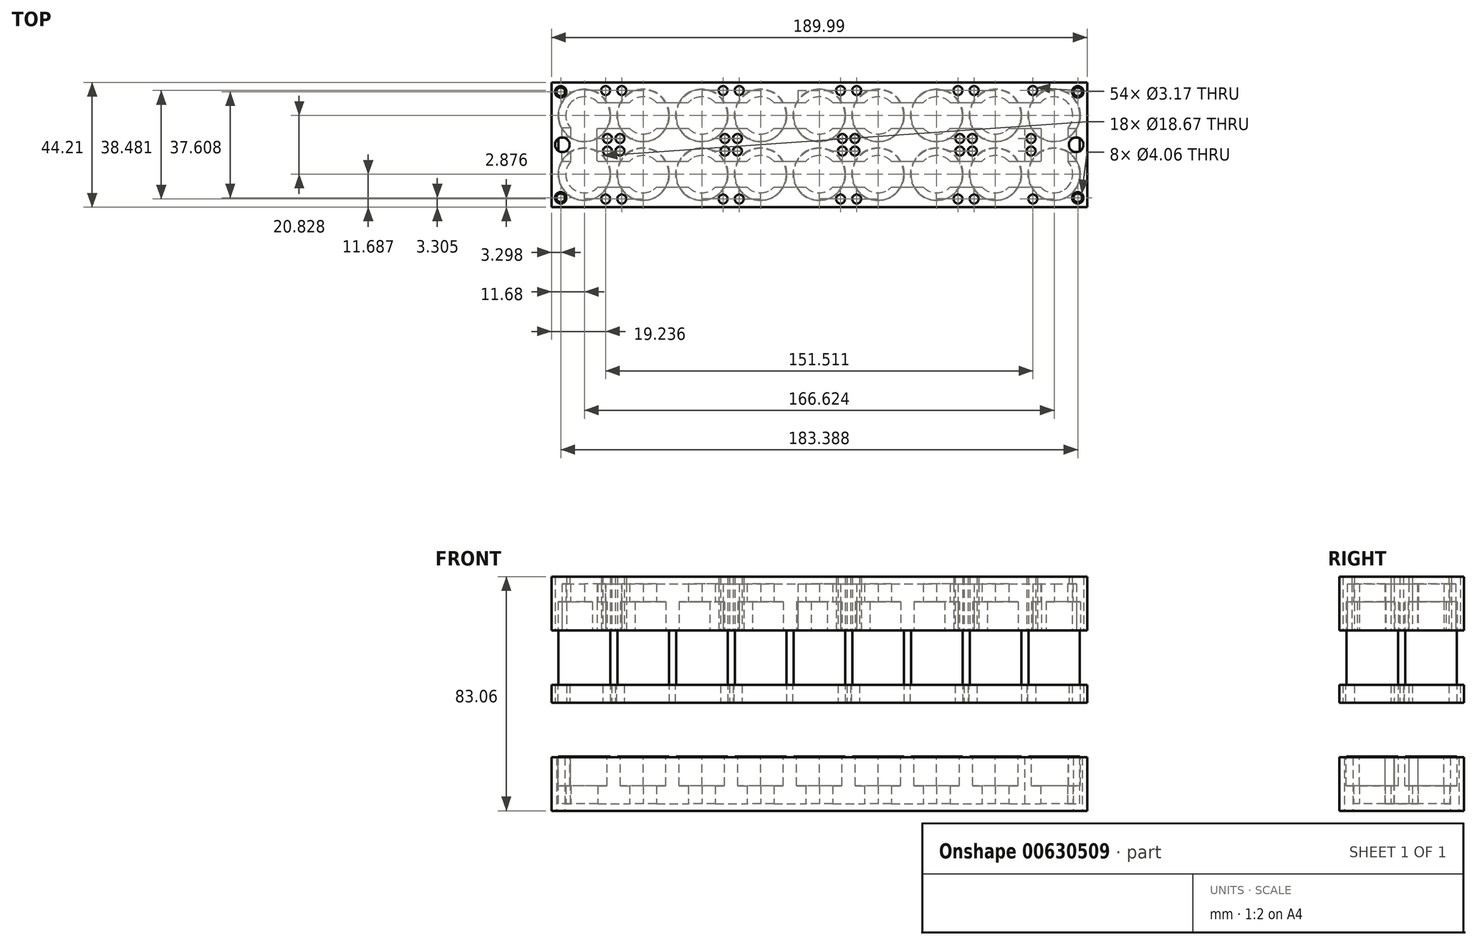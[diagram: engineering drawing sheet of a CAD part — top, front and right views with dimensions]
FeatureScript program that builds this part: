
annotation { "Feature Type Name" : "Feature", "Feature Type Description" : "" }
export const myFeature = defineFeature(function(context is Context, id is Id, definition is map)
    precondition{}
    {
        {
            var Q0;
            Q0=qCreatedBy(makeId("Top.planeOp"),FACE);
            var sketch = newSketch(context, id + "F0", { "sketchPlane" : qUnion([Q0])});
            skCircle(sketch, "E0", {"center": v(0, 0) * mm, "radius": 9.14 * mm});
            skCircle(sketch, "E1.1.0.0", {"center": v(20.83, 0) * mm, "radius": 9.14 * mm});
            skCircle(sketch, "E1.2.0.0", {"center": v(41.66, 0) * mm, "radius": 9.14 * mm});
            skCircle(sketch, "E1.3.0.0", {"center": v(62.48, 0) * mm, "radius": 9.14 * mm});
            skCircle(sketch, "E1.4.0.0", {"center": v(83.31, 0) * mm, "radius": 9.14 * mm});
            skCircle(sketch, "E1.5.0.0", {"center": v(104.14, 0) * mm, "radius": 9.14 * mm});
            skLineSegment(sketch, "E1.direction1", {"start": v(0, 0) * mm, "end": v(20.83, 0) * mm, "construction": true});
            skCircle(sketch, "E2", {"center": v(0, 20.83) * mm, "radius": 9.14 * mm});
            skCircle(sketch, "E3.1.0.0", {"center": v(20.83, 20.83) * mm, "radius": 9.14 * mm});
            skCircle(sketch, "E3.2.0.0", {"center": v(41.66, 20.83) * mm, "radius": 9.14 * mm});
            skCircle(sketch, "E3.3.0.0", {"center": v(62.48, 20.83) * mm, "radius": 9.14 * mm});
            skCircle(sketch, "E3.4.0.0", {"center": v(83.31, 20.83) * mm, "radius": 9.14 * mm});
            skCircle(sketch, "E3.5.0.0", {"center": v(104.14, 20.83) * mm, "radius": 9.14 * mm});
            skLineSegment(sketch, "E3.direction1", {"start": v(0, 20.83) * mm, "end": v(20.83, 20.83) * mm, "construction": true});
            skCircle(sketch, "E4.0.6.0", {"center": v(124.97, 20.83) * mm, "radius": 9.14 * mm});
            skCircle(sketch, "E4.0.7.0", {"center": v(145.8, 20.83) * mm, "radius": 9.14 * mm});
            skCircle(sketch, "E4.0.8.0", {"center": v(166.62, 20.83) * mm, "radius": 9.14 * mm});
            skCircle(sketch, "E5.0.6.0", {"center": v(124.97, 0) * mm, "radius": 9.14 * mm});
            skCircle(sketch, "E5.0.7.0", {"center": v(145.8, 0) * mm, "radius": 9.14 * mm});
            skCircle(sketch, "E5.0.8.0", {"center": v(166.62, 0) * mm, "radius": 9.14 * mm});
            skCircle(sketch, "E6", {"center": v(0, -87.4) * mm, "radius": 6.6 * mm});
            skCircle(sketch, "E7.1.0.0", {"center": v(20.83, -87.4) * mm, "radius": 6.6 * mm});
            skCircle(sketch, "E7.2.0.0", {"center": v(41.66, -87.4) * mm, "radius": 6.6 * mm});
            skCircle(sketch, "E7.3.0.0", {"center": v(62.48, -87.4) * mm, "radius": 6.6 * mm});
            skCircle(sketch, "E7.4.0.0", {"center": v(83.31, -87.4) * mm, "radius": 6.6 * mm});
            skCircle(sketch, "E7.5.0.0", {"center": v(104.14, -87.4) * mm, "radius": 6.6 * mm});
            skLineSegment(sketch, "E7.direction1", {"start": v(0, -87.4) * mm, "end": v(20.83, -87.4) * mm, "construction": true});
            skCircle(sketch, "E8", {"center": v(0, -66.56) * mm, "radius": 6.6 * mm});
            skCircle(sketch, "E9.1.0.0", {"center": v(20.83, -66.56) * mm, "radius": 6.6 * mm});
            skCircle(sketch, "E9.2.0.0", {"center": v(41.66, -66.56) * mm, "radius": 6.6 * mm});
            skCircle(sketch, "E9.3.0.0", {"center": v(62.48, -66.56) * mm, "radius": 6.6 * mm});
            skCircle(sketch, "E9.4.0.0", {"center": v(83.31, -66.56) * mm, "radius": 6.6 * mm});
            skCircle(sketch, "E9.5.0.0", {"center": v(104.14, -66.56) * mm, "radius": 6.6 * mm});
            skLineSegment(sketch, "E9.direction1", {"start": v(0, -66.56) * mm, "end": v(20.83, -66.56) * mm, "construction": true});
            skCircle(sketch, "E10.0.6.0", {"center": v(124.97, -66.56) * mm, "radius": 6.6 * mm});
            skCircle(sketch, "E10.0.7.0", {"center": v(145.8, -66.56) * mm, "radius": 6.6 * mm});
            skCircle(sketch, "E10.0.8.0", {"center": v(166.62, -66.56) * mm, "radius": 6.6 * mm});
            skCircle(sketch, "E11.0.6.0", {"center": v(124.97, -87.4) * mm, "radius": 6.6 * mm});
            skCircle(sketch, "E11.0.7.0", {"center": v(145.8, -87.4) * mm, "radius": 6.6 * mm});
            skCircle(sketch, "E11.0.8.0", {"center": v(166.62, -87.4) * mm, "radius": 6.6 * mm});
            skLineSegment(sketch, "E12.bottom", {"start": v(-11.68, -54.88) * mm, "end": v(178.3, -54.88) * mm});
            skLineSegment(sketch, "E12.top", {"start": v(-11.68, -99.08) * mm, "end": v(178.3, -99.08) * mm});
            skLineSegment(sketch, "E12.left", {"start": v(-11.68, -54.88) * mm, "end": v(-11.68, -99.08) * mm});
            skLineSegment(sketch, "E12.right", {"start": v(178.3, -54.88) * mm, "end": v(178.3, -99.08) * mm});
            skCircle(sketch, "E13", {"center": v(0, -148.51) * mm, "radius": 9.14 * mm});
            skCircle(sketch, "E14.1.0.0", {"center": v(20.83, -148.51) * mm, "radius": 9.14 * mm});
            skCircle(sketch, "E14.2.0.0", {"center": v(41.66, -148.51) * mm, "radius": 9.14 * mm});
            skCircle(sketch, "E14.3.0.0", {"center": v(62.48, -148.51) * mm, "radius": 9.14 * mm});
            skCircle(sketch, "E14.4.0.0", {"center": v(83.31, -148.51) * mm, "radius": 9.14 * mm});
            skCircle(sketch, "E14.5.0.0", {"center": v(104.14, -148.51) * mm, "radius": 9.14 * mm});
            skLineSegment(sketch, "E14.direction1", {"start": v(0, -148.51) * mm, "end": v(20.83, -148.51) * mm, "construction": true});
            skCircle(sketch, "E15", {"center": v(0, -127.68) * mm, "radius": 9.14 * mm});
            skCircle(sketch, "E16.1.0.0", {"center": v(20.83, -127.68) * mm, "radius": 9.14 * mm});
            skCircle(sketch, "E16.2.0.0", {"center": v(41.66, -127.68) * mm, "radius": 9.14 * mm});
            skCircle(sketch, "E16.3.0.0", {"center": v(62.48, -127.68) * mm, "radius": 9.14 * mm});
            skCircle(sketch, "E16.4.0.0", {"center": v(83.31, -127.68) * mm, "radius": 9.14 * mm});
            skCircle(sketch, "E16.5.0.0", {"center": v(104.14, -127.68) * mm, "radius": 9.14 * mm});
            skLineSegment(sketch, "E16.direction1", {"start": v(0, -127.68) * mm, "end": v(20.83, -127.68) * mm, "construction": true});
            skCircle(sketch, "E17.0.6.0", {"center": v(124.97, -127.68) * mm, "radius": 9.14 * mm});
            skCircle(sketch, "E17.0.7.0", {"center": v(145.8, -127.68) * mm, "radius": 9.14 * mm});
            skCircle(sketch, "E17.0.8.0", {"center": v(166.62, -127.68) * mm, "radius": 9.14 * mm});
            skCircle(sketch, "E18.0.6.0", {"center": v(124.97, -148.51) * mm, "radius": 9.14 * mm});
            skCircle(sketch, "E18.0.7.0", {"center": v(145.8, -148.51) * mm, "radius": 9.14 * mm});
            skCircle(sketch, "E18.0.8.0", {"center": v(166.62, -148.51) * mm, "radius": 9.14 * mm});
            skLineSegment(sketch, "E19.bottom", {"start": v(-11.68, -116) * mm, "end": v(178.3, -116) * mm});
            skLineSegment(sketch, "E19.top", {"start": v(-11.68, -160.2) * mm, "end": v(178.3, -160.2) * mm});
            skLineSegment(sketch, "E19.left", {"start": v(-11.68, -116) * mm, "end": v(-11.68, -160.2) * mm});
            skLineSegment(sketch, "E19.right", {"start": v(178.3, -116) * mm, "end": v(178.3, -160.2) * mm});
            skCircle(sketch, "E20", {"center": v(0, -215.22) * mm, "radius": 6.6 * mm});
            skCircle(sketch, "E21.1.0.0", {"center": v(20.83, -215.22) * mm, "radius": 6.6 * mm});
            skCircle(sketch, "E21.2.0.0", {"center": v(41.66, -215.22) * mm, "radius": 6.6 * mm});
            skCircle(sketch, "E21.3.0.0", {"center": v(62.48, -215.22) * mm, "radius": 6.6 * mm});
            skCircle(sketch, "E21.4.0.0", {"center": v(83.31, -215.22) * mm, "radius": 6.6 * mm});
            skCircle(sketch, "E21.5.0.0", {"center": v(104.14, -215.22) * mm, "radius": 6.6 * mm});
            skLineSegment(sketch, "E21.direction1", {"start": v(0, -215.22) * mm, "end": v(20.83, -215.22) * mm, "construction": true});
            skCircle(sketch, "E22", {"center": v(0, -194.4) * mm, "radius": 6.6 * mm});
            skCircle(sketch, "E23.1.0.0", {"center": v(20.83, -194.4) * mm, "radius": 6.6 * mm});
            skCircle(sketch, "E23.2.0.0", {"center": v(41.66, -194.4) * mm, "radius": 6.6 * mm});
            skCircle(sketch, "E23.3.0.0", {"center": v(62.48, -194.4) * mm, "radius": 6.6 * mm});
            skCircle(sketch, "E23.4.0.0", {"center": v(83.31, -194.4) * mm, "radius": 6.6 * mm});
            skCircle(sketch, "E23.5.0.0", {"center": v(104.14, -194.4) * mm, "radius": 6.6 * mm});
            skLineSegment(sketch, "E23.direction1", {"start": v(0, -194.4) * mm, "end": v(20.83, -194.4) * mm, "construction": true});
            skCircle(sketch, "E24.0.6.0", {"center": v(124.97, -194.4) * mm, "radius": 6.6 * mm});
            skCircle(sketch, "E24.0.7.0", {"center": v(145.8, -194.4) * mm, "radius": 6.6 * mm});
            skCircle(sketch, "E24.0.8.0", {"center": v(166.62, -194.4) * mm, "radius": 6.6 * mm});
            skCircle(sketch, "E25.0.6.0", {"center": v(124.97, -215.22) * mm, "radius": 6.6 * mm});
            skCircle(sketch, "E25.0.7.0", {"center": v(145.8, -215.22) * mm, "radius": 6.6 * mm});
            skCircle(sketch, "E25.0.8.0", {"center": v(166.62, -215.22) * mm, "radius": 6.6 * mm});
            skLineSegment(sketch, "E26.bottom", {"start": v(-11.68, -182.71) * mm, "end": v(178.3, -182.71) * mm});
            skLineSegment(sketch, "E26.top", {"start": v(-11.68, -226.9) * mm, "end": v(178.3, -226.9) * mm});
            skLineSegment(sketch, "E26.left", {"start": v(-11.68, -182.71) * mm, "end": v(-11.68, -226.9) * mm});
            skLineSegment(sketch, "E26.right", {"start": v(178.3, -182.71) * mm, "end": v(178.3, -226.9) * mm});
            skLineSegment(sketch, "E27", {"start": v(10.41, -127.68) * mm, "end": v(10.41, -148.51) * mm, "construction": true});
            skLineSegment(sketch, "E28", {"start": v(0, -136.83) * mm, "end": v(0, -139.37) * mm, "construction": true});
            skLineSegment(sketch, "E29", {"start": v(0, -138.1) * mm, "end": v(10.41, -138.1) * mm, "construction": true});
            skLineSegment(sketch, "E30", {"start": v(29.97, -127.68) * mm, "end": v(32.51, -127.68) * mm, "construction": true});
            skLineSegment(sketch, "E31", {"start": v(20.83, -139.37) * mm, "end": v(20.83, -136.83) * mm, "construction": true});
            skLineSegment(sketch, "E32", {"start": v(20.83, -138.1) * mm, "end": v(35.36, -138.1) * mm, "construction": true});
            skLineSegment(sketch, "E33", {"start": v(31.24, -127.68) * mm, "end": v(31.24, -138.1) * mm, "construction": true});
            skLineSegment(sketch, "E34.direction1", {"start": v(10.41, -138.1) * mm, "end": v(31.24, -138.1) * mm, "construction": true});
            skLineSegment(sketch, "E35", {"start": v(3.8, -138.1) * mm, "end": v(-13.67, -138.1) * mm, "construction": true});
            skCircle(sketch, "E36", {"center": v(-7.81, -138.1) * mm, "radius": 2.6 * mm});
            skLineSegment(sketch, "E37", {"start": v(178.3, -138.1) * mm, "end": v(168.43, -138.1) * mm, "construction": true});
            skCircle(sketch, "E38", {"center": v(174.43, -138.1) * mm, "radius": 2.6 * mm});
            skLineSegment(sketch, "E39", {"start": v(178.3, -204.8) * mm, "end": v(164.63, -204.8) * mm, "construction": true});
            skLineSegment(sketch, "E40", {"start": v(-11.68, -204.8) * mm, "end": v(0, -204.8) * mm, "construction": true});
            skCircle(sketch, "E41", {"center": v(-7.81, -204.8) * mm, "radius": 2.6 * mm});
            skCircle(sketch, "E42", {"center": v(174.43, -204.8) * mm, "radius": 2.6 * mm});
            skLineSegment(sketch, "E43", {"start": v(10.41, -194.4) * mm, "end": v(10.41, -215.22) * mm, "construction": true});
            skLineSegment(sketch, "E44", {"start": v(20.83, -194.4) * mm, "end": v(41.66, -194.4) * mm, "construction": true});
            skLineSegment(sketch, "E45", {"start": v(41.66, -194.4) * mm, "end": v(41.66, -215.22) * mm, "construction": true});
            skLineSegment(sketch, "E46", {"start": v(20.83, -215.22) * mm, "end": v(41.66, -215.22) * mm, "construction": true});
            skLineSegment(sketch, "E47", {"start": v(31.24, -194.4) * mm, "end": v(31.24, -215.22) * mm, "construction": true});
            skLineSegment(sketch, "E48", {"start": v(10.41, -204.8) * mm, "end": v(31.24, -204.8) * mm, "construction": true});
            skLineSegment(sketch, "E49", {"start": v(10.41, -204.8) * mm, "end": v(0, -204.8) * mm, "construction": true});
            skLineSegment(sketch, "E50", {"start": v(20.83, -194.4) * mm, "end": v(20.83, -215.22) * mm, "construction": true});
            skLineSegment(sketch, "E51", {"start": v(62.48, -194.4) * mm, "end": v(62.48, -215.22) * mm, "construction": true});
            skLineSegment(sketch, "E52.2.0.1", {"start": v(52.07, -194.4) * mm, "end": v(52.07, -215.22) * mm, "construction": true});
            skLineSegment(sketch, "E52.3.0.1", {"start": v(72.9, -194.4) * mm, "end": v(72.9, -215.22) * mm, "construction": true});
            skLineSegment(sketch, "E52.4.0.1", {"start": v(93.73, -194.4) * mm, "end": v(93.73, -215.22) * mm, "construction": true});
            skLineSegment(sketch, "E52.5.0.1", {"start": v(114.55, -194.4) * mm, "end": v(114.55, -215.22) * mm, "construction": true});
            skLineSegment(sketch, "E52.6.0.1", {"start": v(135.38, -194.4) * mm, "end": v(135.38, -215.22) * mm, "construction": true});
            skLineSegment(sketch, "E52.7.0.1", {"start": v(156.21, -194.4) * mm, "end": v(156.21, -215.22) * mm, "construction": true});
            skLineSegment(sketch, "E52.direction1", {"start": v(10.41, -215.22) * mm, "end": v(31.24, -215.22) * mm, "construction": true});
            skLineSegment(sketch, "E53", {"start": v(156.21, -226.9) * mm, "end": v(156.21, -182.71) * mm, "construction": true});
            skLineSegment(sketch, "E54", {"start": v(10.41, -182.71) * mm, "end": v(10.41, -226.9) * mm, "construction": true});
            skLineSegment(sketch, "E55", {"start": v(83.31, -182.71) * mm, "end": v(83.31, -226.9) * mm, "construction": true});
            skLineSegment(sketch, "E56", {"start": v(0, -221.83) * mm, "end": v(0, -226.9) * mm, "construction": true});
            skLineSegment(sketch, "E57", {"start": v(0, -224.37) * mm, "end": v(156.21, -224.37) * mm, "construction": true});
            skLineSegment(sketch, "E58", {"start": v(166.62, -187.8) * mm, "end": v(166.62, -187.03) * mm, "construction": true});
            skLineSegment(sketch, "E59", {"start": v(-6.6, -194.4) * mm, "end": v(-11.68, -194.4) * mm, "construction": true});
            skPoint(sketch, "E60.startSnap0", {"position": v(-9.14, -194.4) * mm});
            skLineSegment(sketch, "E61", {"start": v(173.23, -194.4) * mm, "end": v(178.3, -194.4) * mm, "construction": true});
            skCircle(sketch, "E62", {"center": v(-8.38, -186.01) * mm, "radius": 2.03 * mm});
            skCircle(sketch, "E63.MirrorC", {"center": v(175, -186.01) * mm, "radius": 2.03 * mm});
            skCircle(sketch, "E64.MirrorC", {"center": v(-8.38, -223.6) * mm, "radius": 2.03 * mm});
            skCircle(sketch, "E65.MirrorC", {"center": v(175, -223.6) * mm, "radius": 2.03 * mm});
            skLineSegment(sketch, "E66", {"start": v(-11.68, -160.2) * mm, "end": v(-11.68, -182.71) * mm, "construction": true});
            skLineSegment(sketch, "E67", {"start": v(178.3, -160.2) * mm, "end": v(178.3, -182.71) * mm, "construction": true});
            skLineSegment(sketch, "E68", {"start": v(178.3, -171.45) * mm, "end": v(-11.68, -171.45) * mm, "construction": true});
            skCircle(sketch, "E69.MirrorC", {"center": v(-8.38, -156.9) * mm, "radius": 2.03 * mm});
            skCircle(sketch, "E70.MirrorC", {"center": v(175, -156.9) * mm, "radius": 2.03 * mm});
            skCircle(sketch, "E71.MirrorC", {"center": v(-8.38, -119.3) * mm, "radius": 2.03 * mm});
            skCircle(sketch, "E72.MirrorC", {"center": v(175, -119.3) * mm, "radius": 2.03 * mm});
            skCircle(sketch, "E73", {"center": v(8.2, -202.59) * mm, "radius": 1.59 * mm});
            skCircle(sketch, "E74", {"center": v(7.56, -185.57) * mm, "radius": 1.59 * mm});
            skCircle(sketch, "E75.MirrorC", {"center": v(8.2, -207.03) * mm, "radius": 1.59 * mm});
            skCircle(sketch, "E76.MirrorC", {"center": v(7.56, -224.05) * mm, "radius": 1.59 * mm});
            skLineSegment(sketch, "E77.MirrorCS", {"start": v(10.41, -226.9) * mm, "end": v(10.41, -182.71) * mm, "construction": true});
            skCircle(sketch, "E78.MirrorC", {"center": v(13.27, -185.57) * mm, "radius": 1.59 * mm});
            skCircle(sketch, "E79.MirrorC", {"center": v(12.64, -202.59) * mm, "radius": 1.59 * mm});
            skCircle(sketch, "E80.MirrorC", {"center": v(12.64, -207.03) * mm, "radius": 1.59 * mm});
            skCircle(sketch, "E81.MirrorC", {"center": v(13.27, -224.05) * mm, "radius": 1.59 * mm});
            skCircle(sketch, "E82.2.0.0", {"center": v(54.93, -224.05) * mm, "radius": 1.59 * mm});
            skCircle(sketch, "E82.2.0.1", {"center": v(49.21, -224.05) * mm, "radius": 1.59 * mm});
            skCircle(sketch, "E82.2.0.2", {"center": v(54.3, -207.03) * mm, "radius": 1.59 * mm});
            skCircle(sketch, "E82.2.0.3", {"center": v(49.85, -207.03) * mm, "radius": 1.59 * mm});
            skCircle(sketch, "E82.2.0.4", {"center": v(49.85, -202.59) * mm, "radius": 1.59 * mm});
            skCircle(sketch, "E82.2.0.5", {"center": v(54.93, -185.57) * mm, "radius": 1.59 * mm});
            skCircle(sketch, "E82.2.0.6", {"center": v(49.21, -185.57) * mm, "radius": 1.59 * mm});
            skCircle(sketch, "E82.2.0.7", {"center": v(54.3, -202.59) * mm, "radius": 1.59 * mm});
            skCircle(sketch, "E82.4.0.0", {"center": v(96.58, -224.05) * mm, "radius": 1.59 * mm});
            skCircle(sketch, "E82.4.0.1", {"center": v(90.87, -224.05) * mm, "radius": 1.59 * mm});
            skCircle(sketch, "E82.4.0.2", {"center": v(95.95, -207.03) * mm, "radius": 1.59 * mm});
            skCircle(sketch, "E82.4.0.3", {"center": v(91.5, -207.03) * mm, "radius": 1.59 * mm});
            skCircle(sketch, "E82.4.0.4", {"center": v(91.5, -202.59) * mm, "radius": 1.59 * mm});
            skCircle(sketch, "E82.4.0.5", {"center": v(96.58, -185.57) * mm, "radius": 1.59 * mm});
            skCircle(sketch, "E82.4.0.6", {"center": v(90.87, -185.57) * mm, "radius": 1.59 * mm});
            skCircle(sketch, "E82.4.0.7", {"center": v(95.95, -202.59) * mm, "radius": 1.59 * mm});
            skCircle(sketch, "E82.6.0.0", {"center": v(138.24, -224.05) * mm, "radius": 1.59 * mm});
            skCircle(sketch, "E82.6.0.1", {"center": v(132.52, -224.05) * mm, "radius": 1.59 * mm});
            skCircle(sketch, "E82.6.0.2", {"center": v(137.6, -207.03) * mm, "radius": 1.59 * mm});
            skCircle(sketch, "E82.6.0.3", {"center": v(133.16, -207.03) * mm, "radius": 1.59 * mm});
            skCircle(sketch, "E82.6.0.4", {"center": v(133.16, -202.59) * mm, "radius": 1.59 * mm});
            skCircle(sketch, "E82.6.0.5", {"center": v(138.24, -185.57) * mm, "radius": 1.59 * mm});
            skCircle(sketch, "E82.6.0.6", {"center": v(132.52, -185.57) * mm, "radius": 1.59 * mm});
            skCircle(sketch, "E82.6.0.7", {"center": v(137.6, -202.59) * mm, "radius": 1.59 * mm});
            skCircle(sketch, "E82.7.0.0", {"center": v(159.07, -224.05) * mm, "radius": 1.59 * mm});
            skCircle(sketch, "E82.7.0.2", {"center": v(158.43, -207.03) * mm, "radius": 1.59 * mm});
            skCircle(sketch, "E82.7.0.5", {"center": v(159.07, -185.57) * mm, "radius": 1.59 * mm});
            skCircle(sketch, "E82.7.0.7", {"center": v(158.43, -202.59) * mm, "radius": 1.59 * mm});
            skLineSegment(sketch, "E82.direction1", {"start": v(7.56, -224.05) * mm, "end": v(28.38, -224.05) * mm, "construction": true});
            skCircle(sketch, "E83.MirrorC", {"center": v(12.64, -140.32) * mm, "radius": 1.59 * mm});
            skCircle(sketch, "E84.MirrorC", {"center": v(8.2, -140.32) * mm, "radius": 1.59 * mm});
            skCircle(sketch, "E85.MirrorC", {"center": v(8.2, -135.88) * mm, "radius": 1.59 * mm});
            skCircle(sketch, "E86.MirrorC", {"center": v(12.64, -135.88) * mm, "radius": 1.59 * mm});
            skCircle(sketch, "E87.MirrorC", {"center": v(54.3, -140.32) * mm, "radius": 1.59 * mm});
            skCircle(sketch, "E88.MirrorC", {"center": v(49.85, -140.32) * mm, "radius": 1.59 * mm});
            skCircle(sketch, "E89.MirrorC", {"center": v(49.85, -135.88) * mm, "radius": 1.59 * mm});
            skCircle(sketch, "E90.MirrorC", {"center": v(54.3, -135.88) * mm, "radius": 1.59 * mm});
            skCircle(sketch, "E91.MirrorC", {"center": v(91.5, -140.32) * mm, "radius": 1.59 * mm});
            skCircle(sketch, "E92.MirrorC", {"center": v(95.95, -140.32) * mm, "radius": 1.59 * mm});
            skCircle(sketch, "E93.MirrorC", {"center": v(95.95, -135.88) * mm, "radius": 1.59 * mm});
            skCircle(sketch, "E94.MirrorC", {"center": v(91.5, -135.88) * mm, "radius": 1.59 * mm});
            skCircle(sketch, "E95.MirrorC", {"center": v(133.16, -140.32) * mm, "radius": 1.59 * mm});
            skCircle(sketch, "E96.MirrorC", {"center": v(137.6, -140.32) * mm, "radius": 1.59 * mm});
            skCircle(sketch, "E97.MirrorC", {"center": v(137.6, -135.88) * mm, "radius": 1.59 * mm});
            skCircle(sketch, "E98.MirrorC", {"center": v(158.43, -140.32) * mm, "radius": 1.59 * mm});
            skCircle(sketch, "E99.MirrorC", {"center": v(158.43, -135.88) * mm, "radius": 1.59 * mm});
            skCircle(sketch, "E100.MirrorC", {"center": v(133.16, -135.88) * mm, "radius": 1.59 * mm});
            skLineSegment(sketch, "E101", {"start": v(-11.68, -99.08) * mm, "end": v(-11.68, -116) * mm, "construction": true});
            skLineSegment(sketch, "E102", {"start": v(178.3, -99.08) * mm, "end": v(178.3, -116) * mm, "construction": true});
            skLineSegment(sketch, "E103", {"start": v(178.3, -107.54) * mm, "end": v(-11.68, -107.54) * mm, "construction": true});
            skCircle(sketch, "E104.MirrorC", {"center": v(-8.38, -95.77) * mm, "radius": 2.03 * mm, "construction": true});
            skCircle(sketch, "E105.MirrorC", {"center": v(-8.38, -58.18) * mm, "radius": 2.03 * mm, "construction": true});
            skCircle(sketch, "E106.MirrorC", {"center": v(175, -58.18) * mm, "radius": 2.03 * mm, "construction": true});
            skCircle(sketch, "E107.MirrorC", {"center": v(175, -95.77) * mm, "radius": 2.03 * mm, "construction": true});
            skCircle(sketch, "E108", {"center": v(-8.38, -58.18) * mm, "radius": 1.52 * mm});
            skCircle(sketch, "E109", {"center": v(-8.38, -95.77) * mm, "radius": 1.52 * mm});
            skCircle(sketch, "E110", {"center": v(175, -95.77) * mm, "radius": 1.52 * mm});
            skCircle(sketch, "E111", {"center": v(175, -58.18) * mm, "radius": 1.52 * mm});
            skSolve(sketch);
        }
        {
            var Q0;
            Q0=makeQuery(id+"F0.imprint","IMPRINT",FACE,{"disambiguationData":[TD([[makeQuery(id+"F0.imprint","IMPRINT",EDGE,{"derivedFrom":sQuery(id+"F0.wireOp",EDGE,"E2")}),1.0]])]});
            var Q1;
            Q1=makeQuery(id+"F0.imprint","IMPRINT",FACE,{"disambiguationData":[TD([[makeQuery(id+"F0.imprint","IMPRINT",EDGE,{"derivedFrom":sQuery(id+"F0.wireOp",EDGE,"E3.1.0.0")}),1.0]])]});
            var Q2;
            Q2=makeQuery(id+"F0.imprint","IMPRINT",FACE,{"disambiguationData":[TD([[makeQuery(id+"F0.imprint","IMPRINT",EDGE,{"derivedFrom":sQuery(id+"F0.wireOp",EDGE,"E3.2.0.0")}),1.0]])]});
            var Q3;
            Q3=makeQuery(id+"F0.imprint","IMPRINT",FACE,{"disambiguationData":[TD([[makeQuery(id+"F0.imprint","IMPRINT",EDGE,{"derivedFrom":sQuery(id+"F0.wireOp",EDGE,"E3.3.0.0")}),1.0]])]});
            var Q4;
            Q4=makeQuery(id+"F0.imprint","IMPRINT",FACE,{"disambiguationData":[TD([[makeQuery(id+"F0.imprint","IMPRINT",EDGE,{"derivedFrom":sQuery(id+"F0.wireOp",EDGE,"E3.4.0.0")}),1.0]])]});
            var Q5;
            Q5=makeQuery(id+"F0.imprint","IMPRINT",FACE,{"disambiguationData":[TD([[makeQuery(id+"F0.imprint","IMPRINT",EDGE,{"derivedFrom":sQuery(id+"F0.wireOp",EDGE,"E3.5.0.0")}),1.0]])]});
            var Q6;
            Q6=makeQuery(id+"F0.imprint","IMPRINT",FACE,{"disambiguationData":[TD([[makeQuery(id+"F0.imprint","IMPRINT",EDGE,{"derivedFrom":sQuery(id+"F0.wireOp",EDGE,"E4.0.6.0")}),1.0]])]});
            var Q7;
            Q7=makeQuery(id+"F0.imprint","IMPRINT",FACE,{"disambiguationData":[TD([[makeQuery(id+"F0.imprint","IMPRINT",EDGE,{"derivedFrom":sQuery(id+"F0.wireOp",EDGE,"E4.0.7.0")}),1.0]])]});
            var Q8;
            Q8=makeQuery(id+"F0.imprint","IMPRINT",FACE,{"disambiguationData":[TD([[makeQuery(id+"F0.imprint","IMPRINT",EDGE,{"derivedFrom":sQuery(id+"F0.wireOp",EDGE,"E4.0.8.0")}),1.0]])]});
            var Q9;
            Q9=makeQuery(id+"F0.imprint","IMPRINT",FACE,{"disambiguationData":[TD([[makeQuery(id+"F0.imprint","IMPRINT",EDGE,{"derivedFrom":sQuery(id+"F0.wireOp",EDGE,"E5.0.8.0")}),1.0]])]});
            var Q10;
            Q10=makeQuery(id+"F0.imprint","IMPRINT",FACE,{"disambiguationData":[TD([[makeQuery(id+"F0.imprint","IMPRINT",EDGE,{"derivedFrom":sQuery(id+"F0.wireOp",EDGE,"E5.0.7.0")}),1.0]])]});
            var Q11;
            Q11=makeQuery(id+"F0.imprint","IMPRINT",FACE,{"disambiguationData":[TD([[makeQuery(id+"F0.imprint","IMPRINT",EDGE,{"derivedFrom":sQuery(id+"F0.wireOp",EDGE,"E5.0.6.0")}),1.0]])]});
            var Q12;
            Q12=makeQuery(id+"F0.imprint","IMPRINT",FACE,{"disambiguationData":[TD([[makeQuery(id+"F0.imprint","IMPRINT",EDGE,{"derivedFrom":sQuery(id+"F0.wireOp",EDGE,"E1.5.0.0")}),1.0]])]});
            var Q13;
            Q13=makeQuery(id+"F0.imprint","IMPRINT",FACE,{"disambiguationData":[TD([[makeQuery(id+"F0.imprint","IMPRINT",EDGE,{"derivedFrom":sQuery(id+"F0.wireOp",EDGE,"E1.4.0.0")}),1.0]])]});
            var Q14;
            Q14=makeQuery(id+"F0.imprint","IMPRINT",FACE,{"disambiguationData":[TD([[makeQuery(id+"F0.imprint","IMPRINT",EDGE,{"derivedFrom":sQuery(id+"F0.wireOp",EDGE,"E1.3.0.0")}),1.0]])]});
            var Q15;
            Q15=makeQuery(id+"F0.imprint","IMPRINT",FACE,{"disambiguationData":[TD([[makeQuery(id+"F0.imprint","IMPRINT",EDGE,{"derivedFrom":sQuery(id+"F0.wireOp",EDGE,"E1.2.0.0")}),1.0]])]});
            var Q16;
            Q16=makeQuery(id+"F0.imprint","IMPRINT",FACE,{"disambiguationData":[TD([[makeQuery(id+"F0.imprint","IMPRINT",EDGE,{"derivedFrom":sQuery(id+"F0.wireOp",EDGE,"E1.1.0.0")}),1.0]])]});
            var Q17;
            Q17=makeQuery(id+"F0.imprint","IMPRINT",FACE,{"disambiguationData":[TD([[makeQuery(id+"F0.imprint","IMPRINT",EDGE,{"derivedFrom":sQuery(id+"F0.wireOp",EDGE,"E0")}),1.0]])]});
            extrude(context, id + "F1", {"entities" : qUnion([Q0, Q1, Q2, Q3, Q4, Q5, Q6, Q7, Q8, Q9, Q10, Q11, Q12, Q13, Q14, Q15, Q16, Q17]), "depth" : 65.28 * mm, "offsetDistance" : 25.4 * mm});
        }
        {
            var Q0;
            Q0=makeQuery(id+"F0.imprint","IMPRINT",FACE,{"disambiguationData":[TD([[makeQuery(id+"F0.imprint","IMPRINT",EDGE,{"derivedFrom":sQuery(id+"F0.wireOp",EDGE,"E6")}),-1.0]])]});
            extrude(context, id + "F2", {"entities" : qUnion([Q0]), "depth" : 19.05 * mm, "offsetDistance" : 25.4 * mm});
        }
        {
            var Q0;
            Q0=makeQuery(id+"F0.imprint","IMPRINT",FACE,{"disambiguationData":[TD([[makeQuery(id+"F0.imprint","IMPRINT",EDGE,{"derivedFrom":sQuery(id+"F0.wireOp",EDGE,"E13")}),-1.0]])]});
            extrude(context, id + "F3", {"entities" : qUnion([Q0]), "depth" : 6.35 * mm, "offsetDistance" : 25.4 * mm});
        }
        {
            var Q0;
            Q0=makeQuery(id+"F0.imprint","IMPRINT",FACE,{"disambiguationData":[TD([[makeQuery(id+"F0.imprint","IMPRINT",EDGE,{"derivedFrom":sQuery(id+"F0.wireOp",EDGE,"E20")}),-1.0]])]});
            extrude(context, id + "F4", {"entities" : qUnion([Q0]), "depth" : 19.05 * mm, "offsetDistance" : 25.4 * mm});
        }
        {
            var Q0;
            Q0=makeQuery(id+"F2.opExtrude","CAP_FACE",FACE,{"disambiguationData":[OSD([sQuery(id+"F0.wireOp",EDGE,"E6"),sQuery(id+"F0.wireOp",EDGE,"E7.1.0.0"),sQuery(id+"F0.wireOp",EDGE,"E7.2.0.0"),sQuery(id+"F0.wireOp",EDGE,"E7.3.0.0"),sQuery(id+"F0.wireOp",EDGE,"E7.4.0.0"),sQuery(id+"F0.wireOp",EDGE,"E7.5.0.0"),sQuery(id+"F0.wireOp",EDGE,"E8"),sQuery(id+"F0.wireOp",EDGE,"E9.1.0.0"),sQuery(id+"F0.wireOp",EDGE,"E9.2.0.0"),sQuery(id+"F0.wireOp",EDGE,"E9.3.0.0"),sQuery(id+"F0.wireOp",EDGE,"E9.4.0.0"),sQuery(id+"F0.wireOp",EDGE,"E9.5.0.0"),sQuery(id+"F0.wireOp",EDGE,"E10.0.6.0"),sQuery(id+"F0.wireOp",EDGE,"E10.0.7.0"),sQuery(id+"F0.wireOp",EDGE,"E10.0.8.0"),sQuery(id+"F0.wireOp",EDGE,"E11.0.6.0"),sQuery(id+"F0.wireOp",EDGE,"E11.0.7.0"),sQuery(id+"F0.wireOp",EDGE,"E11.0.8.0"),sQuery(id+"F0.wireOp",EDGE,"E12.bottom"),sQuery(id+"F0.wireOp",EDGE,"E12.top"),sQuery(id+"F0.wireOp",EDGE,"E12.left"),sQuery(id+"F0.wireOp",EDGE,"E12.right"),sQuery(id+"F0.wireOp",EDGE,"E108"),sQuery(id+"F0.wireOp",EDGE,"E109"),sQuery(id+"F0.wireOp",EDGE,"E110"),sQuery(id+"F0.wireOp",EDGE,"E111")])],"isStart":false});
            var sketch = newSketch(context, id + "F5", { "sketchPlane" : qUnion([Q0])});
            skCircle(sketch, "E112", {"center": v(0, -66.56) * mm, "radius": 9.14 * mm});
            skCircle(sketch, "E113.1.0.0", {"center": v(20.83, -66.56) * mm, "radius": 9.14 * mm});
            skCircle(sketch, "E113.2.0.0", {"center": v(41.66, -66.56) * mm, "radius": 9.14 * mm});
            skCircle(sketch, "E113.3.0.0", {"center": v(62.48, -66.56) * mm, "radius": 9.14 * mm});
            skCircle(sketch, "E113.4.0.0", {"center": v(83.31, -66.56) * mm, "radius": 9.14 * mm});
            skCircle(sketch, "E113.5.0.0", {"center": v(104.14, -66.56) * mm, "radius": 9.14 * mm});
            skCircle(sketch, "E113.6.0.0", {"center": v(124.97, -66.56) * mm, "radius": 9.14 * mm});
            skCircle(sketch, "E113.7.0.0", {"center": v(145.8, -66.56) * mm, "radius": 9.14 * mm});
            skCircle(sketch, "E113.8.0.0", {"center": v(166.62, -66.56) * mm, "radius": 9.14 * mm});
            skLineSegment(sketch, "E113.direction1", {"start": v(0, -66.56) * mm, "end": v(20.83, -66.56) * mm, "construction": true});
            skLineSegment(sketch, "E114", {"start": v(-11.68, -76.98) * mm, "end": v(178.3, -76.98) * mm, "construction": true});
            skCircle(sketch, "E115.MirrorC", {"center": v(0, -87.4) * mm, "radius": 9.14 * mm});
            skCircle(sketch, "E116.1.0.0", {"center": v(20.83, -87.4) * mm, "radius": 9.14 * mm});
            skCircle(sketch, "E116.2.0.0", {"center": v(41.66, -87.4) * mm, "radius": 9.14 * mm});
            skCircle(sketch, "E116.3.0.0", {"center": v(62.48, -87.4) * mm, "radius": 9.14 * mm});
            skCircle(sketch, "E116.4.0.0", {"center": v(83.31, -87.4) * mm, "radius": 9.14 * mm});
            skCircle(sketch, "E116.5.0.0", {"center": v(104.14, -87.4) * mm, "radius": 9.14 * mm});
            skCircle(sketch, "E116.6.0.0", {"center": v(124.97, -87.4) * mm, "radius": 9.14 * mm});
            skCircle(sketch, "E116.7.0.0", {"center": v(145.8, -87.4) * mm, "radius": 9.14 * mm});
            skCircle(sketch, "E116.8.0.0", {"center": v(166.62, -87.4) * mm, "radius": 9.14 * mm});
            skLineSegment(sketch, "E116.direction1", {"start": v(0, -87.4) * mm, "end": v(20.83, -87.4) * mm, "construction": true});
            skSolve(sketch);
        }
        {
            var Q0;
            Q0 = qSketchRegion(id + "F5", true);
            extrude(context, id + "F6", {"entities" : qUnion([Q0]), "operationType" : NewBodyOperationType.REMOVE, "oppositeDirection" : true, "depth" : 10.16 * mm, "offsetDistance" : 25.4 * mm});
        }
        {
            var Q0;
            Q0=makeQuery(id+"F2.opExtrude","CAP_FACE",FACE,{"disambiguationData":[OSD([sQuery(id+"F0.wireOp",EDGE,"E6"),sQuery(id+"F0.wireOp",EDGE,"E7.1.0.0"),sQuery(id+"F0.wireOp",EDGE,"E7.2.0.0"),sQuery(id+"F0.wireOp",EDGE,"E7.3.0.0"),sQuery(id+"F0.wireOp",EDGE,"E7.4.0.0"),sQuery(id+"F0.wireOp",EDGE,"E7.5.0.0"),sQuery(id+"F0.wireOp",EDGE,"E8"),sQuery(id+"F0.wireOp",EDGE,"E9.1.0.0"),sQuery(id+"F0.wireOp",EDGE,"E9.2.0.0"),sQuery(id+"F0.wireOp",EDGE,"E9.3.0.0"),sQuery(id+"F0.wireOp",EDGE,"E9.4.0.0"),sQuery(id+"F0.wireOp",EDGE,"E9.5.0.0"),sQuery(id+"F0.wireOp",EDGE,"E10.0.6.0"),sQuery(id+"F0.wireOp",EDGE,"E10.0.7.0"),sQuery(id+"F0.wireOp",EDGE,"E10.0.8.0"),sQuery(id+"F0.wireOp",EDGE,"E11.0.6.0"),sQuery(id+"F0.wireOp",EDGE,"E11.0.7.0"),sQuery(id+"F0.wireOp",EDGE,"E11.0.8.0"),sQuery(id+"F0.wireOp",EDGE,"E12.bottom"),sQuery(id+"F0.wireOp",EDGE,"E12.top"),sQuery(id+"F0.wireOp",EDGE,"E12.left"),sQuery(id+"F0.wireOp",EDGE,"E12.right"),sQuery(id+"F0.wireOp",EDGE,"E108"),sQuery(id+"F0.wireOp",EDGE,"E109"),sQuery(id+"F0.wireOp",EDGE,"E110"),sQuery(id+"F0.wireOp",EDGE,"E111")])],"isStart":false});
            var sketch = newSketch(context, id + "F7", { "sketchPlane" : qUnion([Q0])});
            skLineSegment(sketch, "E117.bottom", {"start": v(0, -62) * mm, "end": v(166.62, -62) * mm});
            skLineSegment(sketch, "E117.top", {"start": v(0, -71.14) * mm, "end": v(166.62, -71.14) * mm});
            skLineSegment(sketch, "E117.left", {"start": v(0, -62) * mm, "end": v(0, -71.14) * mm});
            skLineSegment(sketch, "E117.right", {"start": v(166.62, -62) * mm, "end": v(166.62, -71.14) * mm});
            skLineSegment(sketch, "E118", {"start": v(-11.68, -76.98) * mm, "end": v(178.3, -76.98) * mm, "construction": true});
            skLineSegment(sketch, "E119.MirrorCS", {"start": v(0, -82.82) * mm, "end": v(166.62, -82.82) * mm});
            skLineSegment(sketch, "E120.MirrorCS", {"start": v(0, -91.96) * mm, "end": v(166.62, -91.96) * mm});
            skLineSegment(sketch, "E121.MirrorCS", {"start": v(0, -91.96) * mm, "end": v(0, -82.82) * mm});
            skLineSegment(sketch, "E122.MirrorCS", {"start": v(166.62, -91.96) * mm, "end": v(166.62, -82.82) * mm});
            skCircle(sketch, "E123", {"center": v(0, -87.4) * mm, "radius": 9.18 * mm});
            skSolve(sketch);
        }
        {
            var Q0;
            Q0 = qSketchRegion(id + "F7", true);
            extrude(context, id + "F8", {"entities" : qUnion([Q0]), "operationType" : NewBodyOperationType.REMOVE, "oppositeDirection" : true, "depth" : 16.5 * mm, "offsetDistance" : 25.4 * mm});
        }
        {
            var Q0;
            Q0=makeQuery(id+"F4.opExtrude","CAP_FACE",FACE,{"disambiguationData":[OSD([sQuery(id+"F0.wireOp",EDGE,"E20"),sQuery(id+"F0.wireOp",EDGE,"E21.1.0.0"),sQuery(id+"F0.wireOp",EDGE,"E21.2.0.0"),sQuery(id+"F0.wireOp",EDGE,"E21.3.0.0"),sQuery(id+"F0.wireOp",EDGE,"E21.4.0.0"),sQuery(id+"F0.wireOp",EDGE,"E21.5.0.0"),sQuery(id+"F0.wireOp",EDGE,"E22"),sQuery(id+"F0.wireOp",EDGE,"E23.1.0.0"),sQuery(id+"F0.wireOp",EDGE,"E23.2.0.0"),sQuery(id+"F0.wireOp",EDGE,"E23.3.0.0"),sQuery(id+"F0.wireOp",EDGE,"E23.4.0.0"),sQuery(id+"F0.wireOp",EDGE,"E23.5.0.0"),sQuery(id+"F0.wireOp",EDGE,"E24.0.6.0"),sQuery(id+"F0.wireOp",EDGE,"E24.0.7.0"),sQuery(id+"F0.wireOp",EDGE,"E24.0.8.0"),sQuery(id+"F0.wireOp",EDGE,"E25.0.6.0"),sQuery(id+"F0.wireOp",EDGE,"E25.0.7.0"),sQuery(id+"F0.wireOp",EDGE,"E25.0.8.0"),sQuery(id+"F0.wireOp",EDGE,"E26.bottom"),sQuery(id+"F0.wireOp",EDGE,"E26.top"),sQuery(id+"F0.wireOp",EDGE,"E26.left"),sQuery(id+"F0.wireOp",EDGE,"E26.right"),sQuery(id+"F0.wireOp",EDGE,"E41"),sQuery(id+"F0.wireOp",EDGE,"E42"),sQuery(id+"F0.wireOp",EDGE,"E62"),sQuery(id+"F0.wireOp",EDGE,"E63.MirrorC"),sQuery(id+"F0.wireOp",EDGE,"E64.MirrorC"),sQuery(id+"F0.wireOp",EDGE,"E65.MirrorC"),sQuery(id+"F0.wireOp",EDGE,"E73"),sQuery(id+"F0.wireOp",EDGE,"E74"),sQuery(id+"F0.wireOp",EDGE,"E75.MirrorC"),sQuery(id+"F0.wireOp",EDGE,"E76.MirrorC"),sQuery(id+"F0.wireOp",EDGE,"E78.MirrorC"),sQuery(id+"F0.wireOp",EDGE,"E79.MirrorC"),sQuery(id+"F0.wireOp",EDGE,"E80.MirrorC"),sQuery(id+"F0.wireOp",EDGE,"E81.MirrorC"),sQuery(id+"F0.wireOp",EDGE,"E82.1.0.0"),sQuery(id+"F0.wireOp",EDGE,"E82.1.0.1"),sQuery(id+"F0.wireOp",EDGE,"E82.1.0.2"),sQuery(id+"F0.wireOp",EDGE,"E82.1.0.3"),sQuery(id+"F0.wireOp",EDGE,"E82.1.0.4"),sQuery(id+"F0.wireOp",EDGE,"E82.1.0.5"),sQuery(id+"F0.wireOp",EDGE,"E82.1.0.6"),sQuery(id+"F0.wireOp",EDGE,"E82.1.0.7"),sQuery(id+"F0.wireOp",EDGE,"E82.2.0.0"),sQuery(id+"F0.wireOp",EDGE,"E82.2.0.1"),sQuery(id+"F0.wireOp",EDGE,"E82.2.0.2"),sQuery(id+"F0.wireOp",EDGE,"E82.2.0.3"),sQuery(id+"F0.wireOp",EDGE,"E82.2.0.4"),sQuery(id+"F0.wireOp",EDGE,"E82.2.0.5"),sQuery(id+"F0.wireOp",EDGE,"E82.2.0.6"),sQuery(id+"F0.wireOp",EDGE,"E82.2.0.7"),sQuery(id+"F0.wireOp",EDGE,"E82.3.0.0"),sQuery(id+"F0.wireOp",EDGE,"E82.3.0.1"),sQuery(id+"F0.wireOp",EDGE,"E82.3.0.2"),sQuery(id+"F0.wireOp",EDGE,"E82.3.0.3"),sQuery(id+"F0.wireOp",EDGE,"E82.3.0.4"),sQuery(id+"F0.wireOp",EDGE,"E82.3.0.5"),sQuery(id+"F0.wireOp",EDGE,"E82.3.0.6"),sQuery(id+"F0.wireOp",EDGE,"E82.3.0.7"),sQuery(id+"F0.wireOp",EDGE,"E82.4.0.0"),sQuery(id+"F0.wireOp",EDGE,"E82.4.0.1"),sQuery(id+"F0.wireOp",EDGE,"E82.4.0.2"),sQuery(id+"F0.wireOp",EDGE,"E82.4.0.3"),sQuery(id+"F0.wireOp",EDGE,"E82.4.0.4"),sQuery(id+"F0.wireOp",EDGE,"E82.4.0.5"),sQuery(id+"F0.wireOp",EDGE,"E82.4.0.6"),sQuery(id+"F0.wireOp",EDGE,"E82.4.0.7"),sQuery(id+"F0.wireOp",EDGE,"E82.5.0.0"),sQuery(id+"F0.wireOp",EDGE,"E82.5.0.1"),sQuery(id+"F0.wireOp",EDGE,"E82.5.0.2"),sQuery(id+"F0.wireOp",EDGE,"E82.5.0.3"),sQuery(id+"F0.wireOp",EDGE,"E82.5.0.4"),sQuery(id+"F0.wireOp",EDGE,"E82.5.0.5"),sQuery(id+"F0.wireOp",EDGE,"E82.5.0.6"),sQuery(id+"F0.wireOp",EDGE,"E82.5.0.7"),sQuery(id+"F0.wireOp",EDGE,"E82.6.0.0"),sQuery(id+"F0.wireOp",EDGE,"E82.6.0.1"),sQuery(id+"F0.wireOp",EDGE,"E82.6.0.2"),sQuery(id+"F0.wireOp",EDGE,"E82.6.0.3"),sQuery(id+"F0.wireOp",EDGE,"E82.6.0.4"),sQuery(id+"F0.wireOp",EDGE,"E82.6.0.5"),sQuery(id+"F0.wireOp",EDGE,"E82.6.0.6"),sQuery(id+"F0.wireOp",EDGE,"E82.6.0.7"),sQuery(id+"F0.wireOp",EDGE,"E82.7.0.0"),sQuery(id+"F0.wireOp",EDGE,"E82.7.0.1"),sQuery(id+"F0.wireOp",EDGE,"E82.7.0.2"),sQuery(id+"F0.wireOp",EDGE,"E82.7.0.3"),sQuery(id+"F0.wireOp",EDGE,"E82.7.0.4"),sQuery(id+"F0.wireOp",EDGE,"E82.7.0.5"),sQuery(id+"F0.wireOp",EDGE,"E82.7.0.6"),sQuery(id+"F0.wireOp",EDGE,"E82.7.0.7")])],"isStart":true});
            var sketch = newSketch(context, id + "F9", { "sketchPlane" : qUnion([Q0])});
            skCircle(sketch, "E124", {"center": v(0, 215.22) * mm, "radius": 9.14 * mm});
            skLineSegment(sketch, "E125", {"start": v(-11.68, 204.8) * mm, "end": v(178.3, 204.8) * mm, "construction": true});
            skCircle(sketch, "E126.1.0.0", {"center": v(20.83, 215.22) * mm, "radius": 9.14 * mm});
            skCircle(sketch, "E126.2.0.0", {"center": v(41.66, 215.22) * mm, "radius": 9.14 * mm});
            skCircle(sketch, "E126.3.0.0", {"center": v(62.48, 215.22) * mm, "radius": 9.14 * mm});
            skCircle(sketch, "E126.4.0.0", {"center": v(83.31, 215.22) * mm, "radius": 9.14 * mm});
            skCircle(sketch, "E126.5.0.0", {"center": v(104.14, 215.22) * mm, "radius": 9.14 * mm});
            skCircle(sketch, "E126.6.0.0", {"center": v(124.97, 215.22) * mm, "radius": 9.14 * mm});
            skCircle(sketch, "E126.7.0.0", {"center": v(145.8, 215.22) * mm, "radius": 9.14 * mm});
            skCircle(sketch, "E126.8.0.0", {"center": v(166.62, 215.22) * mm, "radius": 9.14 * mm});
            skLineSegment(sketch, "E126.direction1", {"start": v(0, 215.22) * mm, "end": v(20.83, 215.22) * mm, "construction": true});
            skCircle(sketch, "E127.MirrorC", {"center": v(0, 194.4) * mm, "radius": 9.14 * mm});
            skCircle(sketch, "E128.MirrorC", {"center": v(20.83, 194.4) * mm, "radius": 9.14 * mm});
            skCircle(sketch, "E129.MirrorC", {"center": v(41.66, 194.4) * mm, "radius": 9.14 * mm});
            skCircle(sketch, "E130.MirrorC", {"center": v(62.48, 194.4) * mm, "radius": 9.14 * mm});
            skCircle(sketch, "E131.MirrorC", {"center": v(83.31, 194.4) * mm, "radius": 9.14 * mm});
            skCircle(sketch, "E132.MirrorC", {"center": v(104.14, 194.4) * mm, "radius": 9.14 * mm});
            skCircle(sketch, "E133.MirrorC", {"center": v(124.97, 194.4) * mm, "radius": 9.14 * mm});
            skCircle(sketch, "E134.MirrorC", {"center": v(145.8, 194.4) * mm, "radius": 9.14 * mm});
            skCircle(sketch, "E135.MirrorC", {"center": v(166.62, 194.4) * mm, "radius": 9.14 * mm});
            skSolve(sketch);
        }
        {
            var Q0;
            Q0 = qSketchRegion(id + "F9", true);
            extrude(context, id + "F10", {"entities" : qUnion([Q0]), "operationType" : NewBodyOperationType.REMOVE, "oppositeDirection" : true, "depth" : 10.16 * mm, "offsetDistance" : 25.4 * mm});
        }
        {
            var Q0;
            Q0=makeQuery(id+"F4.opExtrude","CAP_FACE",FACE,{"disambiguationData":[OSD([sQuery(id+"F0.wireOp",EDGE,"E20"),sQuery(id+"F0.wireOp",EDGE,"E21.1.0.0"),sQuery(id+"F0.wireOp",EDGE,"E21.2.0.0"),sQuery(id+"F0.wireOp",EDGE,"E21.3.0.0"),sQuery(id+"F0.wireOp",EDGE,"E21.4.0.0"),sQuery(id+"F0.wireOp",EDGE,"E21.5.0.0"),sQuery(id+"F0.wireOp",EDGE,"E22"),sQuery(id+"F0.wireOp",EDGE,"E23.1.0.0"),sQuery(id+"F0.wireOp",EDGE,"E23.2.0.0"),sQuery(id+"F0.wireOp",EDGE,"E23.3.0.0"),sQuery(id+"F0.wireOp",EDGE,"E23.4.0.0"),sQuery(id+"F0.wireOp",EDGE,"E23.5.0.0"),sQuery(id+"F0.wireOp",EDGE,"E24.0.6.0"),sQuery(id+"F0.wireOp",EDGE,"E24.0.7.0"),sQuery(id+"F0.wireOp",EDGE,"E24.0.8.0"),sQuery(id+"F0.wireOp",EDGE,"E25.0.6.0"),sQuery(id+"F0.wireOp",EDGE,"E25.0.7.0"),sQuery(id+"F0.wireOp",EDGE,"E25.0.8.0"),sQuery(id+"F0.wireOp",EDGE,"E26.bottom"),sQuery(id+"F0.wireOp",EDGE,"E26.top"),sQuery(id+"F0.wireOp",EDGE,"E26.left"),sQuery(id+"F0.wireOp",EDGE,"E26.right"),sQuery(id+"F0.wireOp",EDGE,"E41"),sQuery(id+"F0.wireOp",EDGE,"E42"),sQuery(id+"F0.wireOp",EDGE,"E62"),sQuery(id+"F0.wireOp",EDGE,"E63.MirrorC"),sQuery(id+"F0.wireOp",EDGE,"E64.MirrorC"),sQuery(id+"F0.wireOp",EDGE,"E65.MirrorC"),sQuery(id+"F0.wireOp",EDGE,"E73"),sQuery(id+"F0.wireOp",EDGE,"E74"),sQuery(id+"F0.wireOp",EDGE,"E75.MirrorC"),sQuery(id+"F0.wireOp",EDGE,"E76.MirrorC"),sQuery(id+"F0.wireOp",EDGE,"E78.MirrorC"),sQuery(id+"F0.wireOp",EDGE,"E79.MirrorC"),sQuery(id+"F0.wireOp",EDGE,"E80.MirrorC"),sQuery(id+"F0.wireOp",EDGE,"E81.MirrorC"),sQuery(id+"F0.wireOp",EDGE,"E82.1.0.0"),sQuery(id+"F0.wireOp",EDGE,"E82.1.0.1"),sQuery(id+"F0.wireOp",EDGE,"E82.1.0.2"),sQuery(id+"F0.wireOp",EDGE,"E82.1.0.3"),sQuery(id+"F0.wireOp",EDGE,"E82.1.0.4"),sQuery(id+"F0.wireOp",EDGE,"E82.1.0.5"),sQuery(id+"F0.wireOp",EDGE,"E82.1.0.6"),sQuery(id+"F0.wireOp",EDGE,"E82.1.0.7"),sQuery(id+"F0.wireOp",EDGE,"E82.2.0.0"),sQuery(id+"F0.wireOp",EDGE,"E82.2.0.1"),sQuery(id+"F0.wireOp",EDGE,"E82.2.0.2"),sQuery(id+"F0.wireOp",EDGE,"E82.2.0.3"),sQuery(id+"F0.wireOp",EDGE,"E82.2.0.4"),sQuery(id+"F0.wireOp",EDGE,"E82.2.0.5"),sQuery(id+"F0.wireOp",EDGE,"E82.2.0.6"),sQuery(id+"F0.wireOp",EDGE,"E82.2.0.7"),sQuery(id+"F0.wireOp",EDGE,"E82.3.0.0"),sQuery(id+"F0.wireOp",EDGE,"E82.3.0.1"),sQuery(id+"F0.wireOp",EDGE,"E82.3.0.2"),sQuery(id+"F0.wireOp",EDGE,"E82.3.0.3"),sQuery(id+"F0.wireOp",EDGE,"E82.3.0.4"),sQuery(id+"F0.wireOp",EDGE,"E82.3.0.5"),sQuery(id+"F0.wireOp",EDGE,"E82.3.0.6"),sQuery(id+"F0.wireOp",EDGE,"E82.3.0.7"),sQuery(id+"F0.wireOp",EDGE,"E82.4.0.0"),sQuery(id+"F0.wireOp",EDGE,"E82.4.0.1"),sQuery(id+"F0.wireOp",EDGE,"E82.4.0.2"),sQuery(id+"F0.wireOp",EDGE,"E82.4.0.3"),sQuery(id+"F0.wireOp",EDGE,"E82.4.0.4"),sQuery(id+"F0.wireOp",EDGE,"E82.4.0.5"),sQuery(id+"F0.wireOp",EDGE,"E82.4.0.6"),sQuery(id+"F0.wireOp",EDGE,"E82.4.0.7"),sQuery(id+"F0.wireOp",EDGE,"E82.5.0.0"),sQuery(id+"F0.wireOp",EDGE,"E82.5.0.1"),sQuery(id+"F0.wireOp",EDGE,"E82.5.0.2"),sQuery(id+"F0.wireOp",EDGE,"E82.5.0.3"),sQuery(id+"F0.wireOp",EDGE,"E82.5.0.4"),sQuery(id+"F0.wireOp",EDGE,"E82.5.0.5"),sQuery(id+"F0.wireOp",EDGE,"E82.5.0.6"),sQuery(id+"F0.wireOp",EDGE,"E82.5.0.7"),sQuery(id+"F0.wireOp",EDGE,"E82.6.0.0"),sQuery(id+"F0.wireOp",EDGE,"E82.6.0.1"),sQuery(id+"F0.wireOp",EDGE,"E82.6.0.2"),sQuery(id+"F0.wireOp",EDGE,"E82.6.0.3"),sQuery(id+"F0.wireOp",EDGE,"E82.6.0.4"),sQuery(id+"F0.wireOp",EDGE,"E82.6.0.5"),sQuery(id+"F0.wireOp",EDGE,"E82.6.0.6"),sQuery(id+"F0.wireOp",EDGE,"E82.6.0.7"),sQuery(id+"F0.wireOp",EDGE,"E82.7.0.0"),sQuery(id+"F0.wireOp",EDGE,"E82.7.0.1"),sQuery(id+"F0.wireOp",EDGE,"E82.7.0.2"),sQuery(id+"F0.wireOp",EDGE,"E82.7.0.3"),sQuery(id+"F0.wireOp",EDGE,"E82.7.0.4"),sQuery(id+"F0.wireOp",EDGE,"E82.7.0.5"),sQuery(id+"F0.wireOp",EDGE,"E82.7.0.6"),sQuery(id+"F0.wireOp",EDGE,"E82.7.0.7")])],"isStart":true});
            var sketch = newSketch(context, id + "F11", { "sketchPlane" : qUnion([Q0])});
            skLineSegment(sketch, "E136.bottom", {"start": v(0, 219.8) * mm, "end": v(167.23, 219.8) * mm});
            skLineSegment(sketch, "E136.top", {"start": v(0, 210.65) * mm, "end": v(167.23, 210.65) * mm});
            skLineSegment(sketch, "E136.left", {"start": v(0, 219.8) * mm, "end": v(0, 210.65) * mm});
            skLineSegment(sketch, "E136.right", {"start": v(167.23, 219.8) * mm, "end": v(167.23, 210.65) * mm});
            skLineSegment(sketch, "E137.bottom", {"start": v(0, 198.97) * mm, "end": v(169.46, 198.97) * mm});
            skLineSegment(sketch, "E137.top", {"start": v(0, 189.82) * mm, "end": v(169.46, 189.82) * mm});
            skLineSegment(sketch, "E137.left", {"start": v(0, 198.97) * mm, "end": v(0, 189.82) * mm});
            skLineSegment(sketch, "E137.right", {"start": v(169.46, 198.97) * mm, "end": v(169.46, 189.82) * mm});
            skSolve(sketch);
        }
        {
            var Q0;
            Q0 = qSketchRegion(id + "F11", true);
            extrude(context, id + "F12", {"entities" : qUnion([Q0]), "operationType" : NewBodyOperationType.REMOVE, "oppositeDirection" : true, "depth" : 16.5 * mm, "offsetDistance" : 25.4 * mm});
        }
        {
            var Q0;
            Q0=makeQuery(id+"F4.opExtrude","CAP_FACE",FACE,{"disambiguationData":[OSD([sQuery(id+"F0.wireOp",EDGE,"E20"),sQuery(id+"F0.wireOp",EDGE,"E21.1.0.0"),sQuery(id+"F0.wireOp",EDGE,"E21.2.0.0"),sQuery(id+"F0.wireOp",EDGE,"E21.3.0.0"),sQuery(id+"F0.wireOp",EDGE,"E21.4.0.0"),sQuery(id+"F0.wireOp",EDGE,"E21.5.0.0"),sQuery(id+"F0.wireOp",EDGE,"E22"),sQuery(id+"F0.wireOp",EDGE,"E23.1.0.0"),sQuery(id+"F0.wireOp",EDGE,"E23.2.0.0"),sQuery(id+"F0.wireOp",EDGE,"E23.3.0.0"),sQuery(id+"F0.wireOp",EDGE,"E23.4.0.0"),sQuery(id+"F0.wireOp",EDGE,"E23.5.0.0"),sQuery(id+"F0.wireOp",EDGE,"E24.0.6.0"),sQuery(id+"F0.wireOp",EDGE,"E24.0.7.0"),sQuery(id+"F0.wireOp",EDGE,"E24.0.8.0"),sQuery(id+"F0.wireOp",EDGE,"E25.0.6.0"),sQuery(id+"F0.wireOp",EDGE,"E25.0.7.0"),sQuery(id+"F0.wireOp",EDGE,"E25.0.8.0"),sQuery(id+"F0.wireOp",EDGE,"E26.bottom"),sQuery(id+"F0.wireOp",EDGE,"E26.top"),sQuery(id+"F0.wireOp",EDGE,"E26.left"),sQuery(id+"F0.wireOp",EDGE,"E26.right"),sQuery(id+"F0.wireOp",EDGE,"E41"),sQuery(id+"F0.wireOp",EDGE,"E42"),sQuery(id+"F0.wireOp",EDGE,"E62"),sQuery(id+"F0.wireOp",EDGE,"E63.MirrorC"),sQuery(id+"F0.wireOp",EDGE,"E64.MirrorC"),sQuery(id+"F0.wireOp",EDGE,"E65.MirrorC"),sQuery(id+"F0.wireOp",EDGE,"E73"),sQuery(id+"F0.wireOp",EDGE,"E74"),sQuery(id+"F0.wireOp",EDGE,"E75.MirrorC"),sQuery(id+"F0.wireOp",EDGE,"E76.MirrorC"),sQuery(id+"F0.wireOp",EDGE,"E78.MirrorC"),sQuery(id+"F0.wireOp",EDGE,"E79.MirrorC"),sQuery(id+"F0.wireOp",EDGE,"E80.MirrorC"),sQuery(id+"F0.wireOp",EDGE,"E81.MirrorC"),sQuery(id+"F0.wireOp",EDGE,"E82.1.0.0"),sQuery(id+"F0.wireOp",EDGE,"E82.1.0.1"),sQuery(id+"F0.wireOp",EDGE,"E82.1.0.2"),sQuery(id+"F0.wireOp",EDGE,"E82.1.0.3"),sQuery(id+"F0.wireOp",EDGE,"E82.1.0.4"),sQuery(id+"F0.wireOp",EDGE,"E82.1.0.5"),sQuery(id+"F0.wireOp",EDGE,"E82.1.0.6"),sQuery(id+"F0.wireOp",EDGE,"E82.1.0.7"),sQuery(id+"F0.wireOp",EDGE,"E82.2.0.0"),sQuery(id+"F0.wireOp",EDGE,"E82.2.0.1"),sQuery(id+"F0.wireOp",EDGE,"E82.2.0.2"),sQuery(id+"F0.wireOp",EDGE,"E82.2.0.3"),sQuery(id+"F0.wireOp",EDGE,"E82.2.0.4"),sQuery(id+"F0.wireOp",EDGE,"E82.2.0.5"),sQuery(id+"F0.wireOp",EDGE,"E82.2.0.6"),sQuery(id+"F0.wireOp",EDGE,"E82.2.0.7"),sQuery(id+"F0.wireOp",EDGE,"E82.3.0.0"),sQuery(id+"F0.wireOp",EDGE,"E82.3.0.1"),sQuery(id+"F0.wireOp",EDGE,"E82.3.0.2"),sQuery(id+"F0.wireOp",EDGE,"E82.3.0.3"),sQuery(id+"F0.wireOp",EDGE,"E82.3.0.4"),sQuery(id+"F0.wireOp",EDGE,"E82.3.0.5"),sQuery(id+"F0.wireOp",EDGE,"E82.3.0.6"),sQuery(id+"F0.wireOp",EDGE,"E82.3.0.7"),sQuery(id+"F0.wireOp",EDGE,"E82.4.0.0"),sQuery(id+"F0.wireOp",EDGE,"E82.4.0.1"),sQuery(id+"F0.wireOp",EDGE,"E82.4.0.2"),sQuery(id+"F0.wireOp",EDGE,"E82.4.0.3"),sQuery(id+"F0.wireOp",EDGE,"E82.4.0.4"),sQuery(id+"F0.wireOp",EDGE,"E82.4.0.5"),sQuery(id+"F0.wireOp",EDGE,"E82.4.0.6"),sQuery(id+"F0.wireOp",EDGE,"E82.4.0.7"),sQuery(id+"F0.wireOp",EDGE,"E82.5.0.0"),sQuery(id+"F0.wireOp",EDGE,"E82.5.0.1"),sQuery(id+"F0.wireOp",EDGE,"E82.5.0.2"),sQuery(id+"F0.wireOp",EDGE,"E82.5.0.3"),sQuery(id+"F0.wireOp",EDGE,"E82.5.0.4"),sQuery(id+"F0.wireOp",EDGE,"E82.5.0.5"),sQuery(id+"F0.wireOp",EDGE,"E82.5.0.6"),sQuery(id+"F0.wireOp",EDGE,"E82.5.0.7"),sQuery(id+"F0.wireOp",EDGE,"E82.6.0.0"),sQuery(id+"F0.wireOp",EDGE,"E82.6.0.1"),sQuery(id+"F0.wireOp",EDGE,"E82.6.0.2"),sQuery(id+"F0.wireOp",EDGE,"E82.6.0.3"),sQuery(id+"F0.wireOp",EDGE,"E82.6.0.4"),sQuery(id+"F0.wireOp",EDGE,"E82.6.0.5"),sQuery(id+"F0.wireOp",EDGE,"E82.6.0.6"),sQuery(id+"F0.wireOp",EDGE,"E82.6.0.7"),sQuery(id+"F0.wireOp",EDGE,"E82.7.0.0"),sQuery(id+"F0.wireOp",EDGE,"E82.7.0.1"),sQuery(id+"F0.wireOp",EDGE,"E82.7.0.2"),sQuery(id+"F0.wireOp",EDGE,"E82.7.0.3"),sQuery(id+"F0.wireOp",EDGE,"E82.7.0.4"),sQuery(id+"F0.wireOp",EDGE,"E82.7.0.5"),sQuery(id+"F0.wireOp",EDGE,"E82.7.0.6"),sQuery(id+"F0.wireOp",EDGE,"E82.7.0.7")])],"isStart":true});
            var sketch = newSketch(context, id + "F13", { "sketchPlane" : qUnion([Q0])});
            skLineSegment(sketch, "E138.bottom", {"start": v(162.05, 214.95) * mm, "end": v(171.2, 214.95) * mm});
            skLineSegment(sketch, "E138.top", {"start": v(162.05, 194.14) * mm, "end": v(171.2, 194.14) * mm});
            skLineSegment(sketch, "E138.left", {"start": v(171.2, 214.95) * mm, "end": v(171.2, 194.14) * mm});
            skLineSegment(sketch, "E138.right", {"start": v(162.05, 214.95) * mm, "end": v(162.05, 194.14) * mm});
            skLineSegment(sketch, "E139.bottom", {"start": v(-4.57, 215.74) * mm, "end": v(4.57, 215.74) * mm});
            skLineSegment(sketch, "E139.top", {"start": v(-4.57, 194.14) * mm, "end": v(4.57, 194.14) * mm});
            skLineSegment(sketch, "E139.left", {"start": v(-4.57, 215.74) * mm, "end": v(-4.57, 194.14) * mm});
            skLineSegment(sketch, "E139.right", {"start": v(4.57, 215.74) * mm, "end": v(4.57, 194.14) * mm});
            skLineSegment(sketch, "E140.bottom", {"start": v(7.56, 224.05) * mm, "end": v(0, 224.05) * mm});
            skLineSegment(sketch, "E140.top", {"start": v(7.56, 219.12) * mm, "end": v(0, 219.12) * mm});
            skLineSegment(sketch, "E140.left", {"start": v(7.56, 224.05) * mm, "end": v(7.56, 219.12) * mm});
            skLineSegment(sketch, "E140.right", {"start": v(0, 224.05) * mm, "end": v(0, 219.12) * mm});
            skLineSegment(sketch, "E141", {"start": v(-11.68, 204.8) * mm, "end": v(82.05, 204.8) * mm, "construction": true});
            skLineSegment(sketch, "E142.MirrorCS", {"start": v(7.56, 185.57) * mm, "end": v(0, 185.57) * mm});
            skLineSegment(sketch, "E143.MirrorCS", {"start": v(0, 185.57) * mm, "end": v(0, 190.5) * mm});
            skLineSegment(sketch, "E144.MirrorCS", {"start": v(7.56, 190.5) * mm, "end": v(0, 190.5) * mm});
            skLineSegment(sketch, "E145.MirrorCS", {"start": v(7.56, 185.57) * mm, "end": v(7.56, 190.5) * mm});
            skLineSegment(sketch, "E146", {"start": v(13.27, 224.05) * mm, "end": v(7.56, 224.05) * mm, "construction": true});
            skLineSegment(sketch, "E147", {"start": v(10.41, 224.05) * mm, "end": v(10.41, 214.4) * mm, "construction": true});
            skLineSegment(sketch, "E148.MirrorCS", {"start": v(13.27, 224.05) * mm, "end": v(13.27, 219.12) * mm});
            skLineSegment(sketch, "E149.MirrorCS", {"start": v(13.27, 219.12) * mm, "end": v(20.83, 219.12) * mm});
            skLineSegment(sketch, "E150.MirrorCS", {"start": v(13.27, 224.05) * mm, "end": v(20.83, 224.05) * mm});
            skLineSegment(sketch, "E151.MirrorCS", {"start": v(20.83, 224.05) * mm, "end": v(20.83, 219.12) * mm});
            skLineSegment(sketch, "E152.MirrorCS", {"start": v(13.27, 190.5) * mm, "end": v(20.83, 190.5) * mm});
            skLineSegment(sketch, "E153.MirrorCS", {"start": v(20.83, 185.57) * mm, "end": v(20.83, 190.5) * mm});
            skLineSegment(sketch, "E154.MirrorCS", {"start": v(13.27, 185.57) * mm, "end": v(20.83, 185.57) * mm});
            skLineSegment(sketch, "E155.MirrorCS", {"start": v(13.27, 185.57) * mm, "end": v(13.27, 190.5) * mm});
            skLineSegment(sketch, "E156.1.0.3", {"start": v(41.66, 224.05) * mm, "end": v(41.66, 219.12) * mm});
            skLineSegment(sketch, "E156.1.0.15", {"start": v(41.66, 185.57) * mm, "end": v(41.66, 190.5) * mm});
            skLineSegment(sketch, "E156.2.0.0", {"start": v(54.93, 224.05) * mm, "end": v(62.48, 224.05) * mm});
            skLineSegment(sketch, "E156.2.0.1", {"start": v(54.93, 219.12) * mm, "end": v(62.48, 219.12) * mm});
            skLineSegment(sketch, "E156.2.0.2", {"start": v(54.93, 224.05) * mm, "end": v(54.93, 219.12) * mm});
            skLineSegment(sketch, "E156.2.0.3", {"start": v(62.48, 224.05) * mm, "end": v(62.48, 219.12) * mm});
            skLineSegment(sketch, "E156.2.0.4", {"start": v(41.66, 224.05) * mm, "end": v(41.66, 219.12) * mm});
            skLineSegment(sketch, "E156.2.0.5", {"start": v(49.21, 219.12) * mm, "end": v(41.66, 219.12) * mm});
            skLineSegment(sketch, "E156.2.0.6", {"start": v(49.21, 224.05) * mm, "end": v(41.66, 224.05) * mm});
            skLineSegment(sketch, "E156.2.0.7", {"start": v(49.21, 224.05) * mm, "end": v(49.21, 219.12) * mm});
            skLineSegment(sketch, "E156.2.0.8", {"start": v(49.21, 190.5) * mm, "end": v(41.66, 190.5) * mm});
            skLineSegment(sketch, "E156.2.0.9", {"start": v(41.66, 185.57) * mm, "end": v(41.66, 190.5) * mm});
            skLineSegment(sketch, "E156.2.0.10", {"start": v(49.21, 185.57) * mm, "end": v(49.21, 190.5) * mm});
            skLineSegment(sketch, "E156.2.0.11", {"start": v(49.21, 185.57) * mm, "end": v(41.66, 185.57) * mm});
            skLineSegment(sketch, "E156.2.0.12", {"start": v(54.93, 190.5) * mm, "end": v(62.48, 190.5) * mm});
            skLineSegment(sketch, "E156.2.0.13", {"start": v(54.93, 185.57) * mm, "end": v(54.93, 190.5) * mm});
            skLineSegment(sketch, "E156.2.0.14", {"start": v(54.93, 185.57) * mm, "end": v(62.48, 185.57) * mm});
            skLineSegment(sketch, "E156.2.0.15", {"start": v(62.48, 185.57) * mm, "end": v(62.48, 190.5) * mm});
            skLineSegment(sketch, "E156.3.0.3", {"start": v(83.31, 224.05) * mm, "end": v(83.31, 219.12) * mm});
            skLineSegment(sketch, "E156.3.0.4", {"start": v(62.48, 224.05) * mm, "end": v(62.48, 219.12) * mm});
            skLineSegment(sketch, "E156.3.0.9", {"start": v(62.48, 185.57) * mm, "end": v(62.48, 190.5) * mm});
            skLineSegment(sketch, "E156.3.0.12", {"start": v(75.76, 190.5) * mm, "end": v(83.31, 190.5) * mm});
            skLineSegment(sketch, "E156.3.0.13", {"start": v(75.76, 185.57) * mm, "end": v(75.76, 190.5) * mm});
            skLineSegment(sketch, "E156.3.0.14", {"start": v(75.76, 185.57) * mm, "end": v(83.31, 185.57) * mm});
            skLineSegment(sketch, "E156.3.0.15", {"start": v(83.31, 185.57) * mm, "end": v(83.31, 190.5) * mm});
            skLineSegment(sketch, "E156.4.0.0", {"start": v(96.58, 224.05) * mm, "end": v(104.14, 224.05) * mm});
            skLineSegment(sketch, "E156.4.0.1", {"start": v(96.58, 219.12) * mm, "end": v(104.14, 219.12) * mm});
            skLineSegment(sketch, "E156.4.0.2", {"start": v(96.58, 224.05) * mm, "end": v(96.58, 219.12) * mm});
            skLineSegment(sketch, "E156.4.0.3", {"start": v(104.14, 224.05) * mm, "end": v(104.14, 219.12) * mm});
            skLineSegment(sketch, "E156.4.0.4", {"start": v(83.31, 224.05) * mm, "end": v(83.31, 219.12) * mm});
            skLineSegment(sketch, "E156.4.0.5", {"start": v(90.87, 219.12) * mm, "end": v(83.31, 219.12) * mm});
            skLineSegment(sketch, "E156.4.0.6", {"start": v(90.87, 224.05) * mm, "end": v(83.31, 224.05) * mm});
            skLineSegment(sketch, "E156.4.0.7", {"start": v(90.87, 224.05) * mm, "end": v(90.87, 219.12) * mm});
            skLineSegment(sketch, "E156.4.0.8", {"start": v(90.87, 190.5) * mm, "end": v(83.31, 190.5) * mm});
            skLineSegment(sketch, "E156.4.0.9", {"start": v(83.31, 185.57) * mm, "end": v(83.31, 190.5) * mm});
            skLineSegment(sketch, "E156.4.0.10", {"start": v(90.87, 185.57) * mm, "end": v(90.87, 190.5) * mm});
            skLineSegment(sketch, "E156.4.0.11", {"start": v(90.87, 185.57) * mm, "end": v(83.31, 185.57) * mm});
            skLineSegment(sketch, "E156.4.0.12", {"start": v(96.58, 190.5) * mm, "end": v(104.14, 190.5) * mm});
            skLineSegment(sketch, "E156.4.0.13", {"start": v(96.58, 185.57) * mm, "end": v(96.58, 190.5) * mm});
            skLineSegment(sketch, "E156.4.0.14", {"start": v(96.58, 185.57) * mm, "end": v(104.14, 185.57) * mm});
            skLineSegment(sketch, "E156.4.0.15", {"start": v(104.14, 185.57) * mm, "end": v(104.14, 190.5) * mm});
            skLineSegment(sketch, "E156.5.0.3", {"start": v(124.97, 224.05) * mm, "end": v(124.97, 219.12) * mm});
            skLineSegment(sketch, "E156.5.0.4", {"start": v(104.14, 224.05) * mm, "end": v(104.14, 219.12) * mm});
            skLineSegment(sketch, "E156.5.0.9", {"start": v(104.14, 185.57) * mm, "end": v(104.14, 190.5) * mm});
            skLineSegment(sketch, "E156.5.0.15", {"start": v(124.97, 185.57) * mm, "end": v(124.97, 190.5) * mm});
            skLineSegment(sketch, "E156.6.0.0", {"start": v(138.24, 224.05) * mm, "end": v(145.8, 224.05) * mm});
            skLineSegment(sketch, "E156.6.0.1", {"start": v(138.24, 219.12) * mm, "end": v(145.8, 219.12) * mm});
            skLineSegment(sketch, "E156.6.0.2", {"start": v(138.24, 224.05) * mm, "end": v(138.24, 219.12) * mm});
            skLineSegment(sketch, "E156.6.0.3", {"start": v(145.8, 224.05) * mm, "end": v(145.8, 219.12) * mm});
            skLineSegment(sketch, "E156.6.0.4", {"start": v(124.97, 224.05) * mm, "end": v(124.97, 219.12) * mm});
            skLineSegment(sketch, "E156.6.0.5", {"start": v(132.52, 219.12) * mm, "end": v(124.97, 219.12) * mm});
            skLineSegment(sketch, "E156.6.0.6", {"start": v(132.52, 224.05) * mm, "end": v(124.97, 224.05) * mm});
            skLineSegment(sketch, "E156.6.0.7", {"start": v(132.52, 224.05) * mm, "end": v(132.52, 219.12) * mm});
            skLineSegment(sketch, "E156.6.0.8", {"start": v(132.52, 190.5) * mm, "end": v(124.97, 190.5) * mm});
            skLineSegment(sketch, "E156.6.0.9", {"start": v(124.97, 185.57) * mm, "end": v(124.97, 190.5) * mm});
            skLineSegment(sketch, "E156.6.0.10", {"start": v(132.52, 185.57) * mm, "end": v(132.52, 190.5) * mm});
            skLineSegment(sketch, "E156.6.0.11", {"start": v(132.52, 185.57) * mm, "end": v(124.97, 185.57) * mm});
            skLineSegment(sketch, "E156.6.0.12", {"start": v(138.24, 190.5) * mm, "end": v(145.8, 190.5) * mm});
            skLineSegment(sketch, "E156.6.0.13", {"start": v(138.24, 185.57) * mm, "end": v(138.24, 190.5) * mm});
            skLineSegment(sketch, "E156.6.0.14", {"start": v(138.24, 185.57) * mm, "end": v(145.8, 185.57) * mm});
            skLineSegment(sketch, "E156.6.0.15", {"start": v(145.8, 185.57) * mm, "end": v(145.8, 190.5) * mm});
            skLineSegment(sketch, "E156.7.0.0", {"start": v(159.07, 224.05) * mm, "end": v(166.62, 224.05) * mm});
            skLineSegment(sketch, "E156.7.0.1", {"start": v(159.07, 219.12) * mm, "end": v(166.62, 219.12) * mm});
            skLineSegment(sketch, "E156.7.0.2", {"start": v(159.07, 224.05) * mm, "end": v(159.07, 219.12) * mm});
            skLineSegment(sketch, "E156.7.0.3", {"start": v(166.62, 224.05) * mm, "end": v(166.62, 219.12) * mm});
            skLineSegment(sketch, "E156.7.0.4", {"start": v(145.8, 224.05) * mm, "end": v(145.8, 219.12) * mm});
            skLineSegment(sketch, "E156.7.0.9", {"start": v(145.8, 185.57) * mm, "end": v(145.8, 190.5) * mm});
            skLineSegment(sketch, "E156.7.0.12", {"start": v(159.07, 190.5) * mm, "end": v(166.62, 190.5) * mm});
            skLineSegment(sketch, "E156.7.0.13", {"start": v(159.07, 185.57) * mm, "end": v(159.07, 190.5) * mm});
            skLineSegment(sketch, "E156.7.0.14", {"start": v(159.07, 185.57) * mm, "end": v(166.62, 185.57) * mm});
            skLineSegment(sketch, "E156.7.0.15", {"start": v(166.62, 185.57) * mm, "end": v(166.62, 190.5) * mm});
            skLineSegment(sketch, "E157.bottom", {"start": v(-4.57, 210.74) * mm, "end": v(-7.96, 210.74) * mm});
            skLineSegment(sketch, "E157.top", {"start": v(-4.57, 198.9) * mm, "end": v(-7.96, 198.9) * mm});
            skLineSegment(sketch, "E157.left", {"start": v(-4.57, 210.74) * mm, "end": v(-4.57, 198.9) * mm});
            skLineSegment(sketch, "E157.right", {"start": v(-7.96, 210.74) * mm, "end": v(-7.96, 198.9) * mm});
            skLineSegment(sketch, "E158.bottom", {"start": v(171.2, 210.65) * mm, "end": v(174.54, 210.65) * mm});
            skLineSegment(sketch, "E158.top", {"start": v(171.2, 198.97) * mm, "end": v(174.54, 198.97) * mm});
            skLineSegment(sketch, "E158.left", {"start": v(171.2, 210.65) * mm, "end": v(171.2, 198.97) * mm});
            skLineSegment(sketch, "E158.right", {"start": v(174.54, 210.65) * mm, "end": v(174.54, 198.97) * mm});
            skSolve(sketch);
        }
        {
            var Q0;
            Q0 = qSketchRegion(id + "F13", true);
            extrude(context, id + "F14", {"entities" : qUnion([Q0]), "operationType" : NewBodyOperationType.REMOVE, "oppositeDirection" : true, "depth" : 16.5 * mm, "offsetDistance" : 25.4 * mm});
        }
        {
            var Q0;
            {var subQ0=sQuery(id+"F7.wireOp",EDGE,"E120.MirrorCS");var subQ1=sQuery(id+"F7.wireOp",EDGE,"E123");var subQ2=sQuery(id+"F7.wireOp",EDGE,"E119.MirrorCS");Q0=makeQuery(id+"F8.boolean.opBoolean","COPY",FACE,{"disambiguationData":[TD([makeQuery(id+"F2.opExtrude","SWEPT_FACE",FACE,{"disambiguationData":[OSD([sQuery(id+"F0.wireOp",EDGE,"E6")])]}),makeQuery(id+"F2.opExtrude","SWEPT_FACE",FACE,{"disambiguationData":[OSD([sQuery(id+"F0.wireOp",EDGE,"E7.1.0.0")])]}),makeQuery(id+"F8.opExtrude","SWEPT_FACE",FACE,{"disambiguationData":[OSD([subQ2])]}),makeQuery(id+"F8.opExtrude","SWEPT_FACE",FACE,{"disambiguationData":[OSD([subQ0])]}),makeQuery(id+"F8.opExtrude","SWEPT_FACE",FACE,{"disambiguationData":[OSD([subQ1])]})])],"derivedFrom":makeQuery(id+"F8.opExtrude","CAP_FACE",FACE,{"disambiguationData":[OSD([subQ2,subQ0,sQuery(id+"F7.wireOp",EDGE,"E122.MirrorCS"),subQ1])],"isStart":false})});}
            extrude(context, id + "F15", {"entities" : qUnion([Q0]), "operationType" : NewBodyOperationType.ADD, "depth" : 6.35 * mm, "offsetDistance" : 25.4 * mm});
        }
        {
            var Q0;
            Q0=makeQuery(id+"F2.opExtrude","CAP_FACE",FACE,{"disambiguationData":[OSD([sQuery(id+"F0.wireOp",EDGE,"E6"),sQuery(id+"F0.wireOp",EDGE,"E7.1.0.0"),sQuery(id+"F0.wireOp",EDGE,"E7.2.0.0"),sQuery(id+"F0.wireOp",EDGE,"E7.3.0.0"),sQuery(id+"F0.wireOp",EDGE,"E7.4.0.0"),sQuery(id+"F0.wireOp",EDGE,"E7.5.0.0"),sQuery(id+"F0.wireOp",EDGE,"E8"),sQuery(id+"F0.wireOp",EDGE,"E9.1.0.0"),sQuery(id+"F0.wireOp",EDGE,"E9.2.0.0"),sQuery(id+"F0.wireOp",EDGE,"E9.3.0.0"),sQuery(id+"F0.wireOp",EDGE,"E9.4.0.0"),sQuery(id+"F0.wireOp",EDGE,"E9.5.0.0"),sQuery(id+"F0.wireOp",EDGE,"E10.0.6.0"),sQuery(id+"F0.wireOp",EDGE,"E10.0.7.0"),sQuery(id+"F0.wireOp",EDGE,"E10.0.8.0"),sQuery(id+"F0.wireOp",EDGE,"E11.0.6.0"),sQuery(id+"F0.wireOp",EDGE,"E11.0.7.0"),sQuery(id+"F0.wireOp",EDGE,"E11.0.8.0"),sQuery(id+"F0.wireOp",EDGE,"E12.bottom"),sQuery(id+"F0.wireOp",EDGE,"E12.top"),sQuery(id+"F0.wireOp",EDGE,"E12.left"),sQuery(id+"F0.wireOp",EDGE,"E12.right"),sQuery(id+"F0.wireOp",EDGE,"E108"),sQuery(id+"F0.wireOp",EDGE,"E109"),sQuery(id+"F0.wireOp",EDGE,"E110"),sQuery(id+"F0.wireOp",EDGE,"E111")])],"isStart":false});
            var sketch = newSketch(context, id + "F16", { "sketchPlane" : qUnion([Q0])});
            skLineSegment(sketch, "E159.bottom", {"start": v(1.9, -82.82) * mm, "end": v(20.43, -82.82) * mm});
            skLineSegment(sketch, "E159.top", {"start": v(1.9, -91.96) * mm, "end": v(20.43, -91.96) * mm});
            skLineSegment(sketch, "E159.left", {"start": v(1.9, -82.82) * mm, "end": v(1.9, -91.96) * mm});
            skLineSegment(sketch, "E159.right", {"start": v(20.43, -82.82) * mm, "end": v(20.43, -91.96) * mm});
            skSolve(sketch);
        }
        {
            var Q0;
            Q0 = qSketchRegion(id + "F16", true);
            extrude(context, id + "F17", {"entities" : qUnion([Q0]), "operationType" : NewBodyOperationType.REMOVE, "depth" : 16.5 * mm, "offsetDistance" : 25.4 * mm});
        }
        {
            var Q0;
            {var subQ0=sQuery(id+"F7.wireOp",EDGE,"E120.MirrorCS");var subQ1=sQuery(id+"F7.wireOp",EDGE,"E119.MirrorCS");var subQ3=sQuery(id+"F5.wireOp",EDGE,"E116.1.0.0");var subQ5=makeQuery(id+"F6.boolean.opBoolean","COPY",FACE,{"derivedFrom":makeQuery(id+"F6.opExtrude","CAP_FACE",FACE,{"disambiguationData":[OSD([subQ3])],"isStart":false})});Q0=makeQuery(id+"F15.boolean.opBoolean","MERGE",FACE,{"derivedFrom":[makeQuery(id+"F8.boolean.opBoolean","SPLIT",FACE,{"disambiguationData":[TD([makeQuery(id+"F8.opExtrude","SWEPT_FACE",FACE,{"disambiguationData":[OSD([subQ1])]})])],"derivedFrom":subQ5}),makeQuery(id+"F8.boolean.opBoolean","SPLIT",FACE,{"disambiguationData":[TD([makeQuery(id+"F8.opExtrude","SWEPT_FACE",FACE,{"disambiguationData":[OSD([subQ0])]})])],"derivedFrom":subQ5}),makeQuery(id+"F15.opExtrude","CAP_FACE",FACE,{"disambiguationData":[OSD([subQ1,subQ0,sQuery(id+"F7.wireOp",EDGE,"E122.MirrorCS"),sQuery(id+"F7.wireOp",EDGE,"E123")])],"isStart":false})]});}
            var sketch = newSketch(context, id + "F18", { "sketchPlane" : qUnion([Q0])});
            skLineSegment(sketch, "E160.bottom", {"start": v(0, -82.82) * mm, "end": v(20.77, -82.82) * mm});
            skLineSegment(sketch, "E160.top", {"start": v(0, -91.96) * mm, "end": v(20.77, -91.96) * mm});
            skLineSegment(sketch, "E160.left", {"start": v(0, -82.82) * mm, "end": v(0, -91.96) * mm});
            skLineSegment(sketch, "E160.right", {"start": v(20.77, -82.82) * mm, "end": v(20.77, -91.96) * mm});
            skSolve(sketch);
        }
        {
            var Q0;
            Q0 = qSketchRegion(id + "F18", true);
            extrude(context, id + "F19", {"entities" : qUnion([Q0]), "operationType" : NewBodyOperationType.REMOVE, "oppositeDirection" : true, "depth" : 6.35 * mm, "offsetDistance" : 25.4 * mm});
        }
        {
            var Q0;
            Q0=makeQuery(id+"F2.opExtrude","CAP_FACE",FACE,{"disambiguationData":[OSD([sQuery(id+"F0.wireOp",EDGE,"E6"),sQuery(id+"F0.wireOp",EDGE,"E7.1.0.0"),sQuery(id+"F0.wireOp",EDGE,"E7.2.0.0"),sQuery(id+"F0.wireOp",EDGE,"E7.3.0.0"),sQuery(id+"F0.wireOp",EDGE,"E7.4.0.0"),sQuery(id+"F0.wireOp",EDGE,"E7.5.0.0"),sQuery(id+"F0.wireOp",EDGE,"E8"),sQuery(id+"F0.wireOp",EDGE,"E9.1.0.0"),sQuery(id+"F0.wireOp",EDGE,"E9.2.0.0"),sQuery(id+"F0.wireOp",EDGE,"E9.3.0.0"),sQuery(id+"F0.wireOp",EDGE,"E9.4.0.0"),sQuery(id+"F0.wireOp",EDGE,"E9.5.0.0"),sQuery(id+"F0.wireOp",EDGE,"E10.0.6.0"),sQuery(id+"F0.wireOp",EDGE,"E10.0.7.0"),sQuery(id+"F0.wireOp",EDGE,"E10.0.8.0"),sQuery(id+"F0.wireOp",EDGE,"E11.0.6.0"),sQuery(id+"F0.wireOp",EDGE,"E11.0.7.0"),sQuery(id+"F0.wireOp",EDGE,"E11.0.8.0"),sQuery(id+"F0.wireOp",EDGE,"E12.bottom"),sQuery(id+"F0.wireOp",EDGE,"E12.top"),sQuery(id+"F0.wireOp",EDGE,"E12.left"),sQuery(id+"F0.wireOp",EDGE,"E12.right"),sQuery(id+"F0.wireOp",EDGE,"E108"),sQuery(id+"F0.wireOp",EDGE,"E109"),sQuery(id+"F0.wireOp",EDGE,"E110"),sQuery(id+"F0.wireOp",EDGE,"E111")])],"isStart":false});
            var sketch = newSketch(context, id + "F20", { "sketchPlane" : qUnion([Q0])});
            skLineSegment(sketch, "E161.bottom", {"start": v(-4.93, -71.14) * mm, "end": v(4.95, -71.14) * mm});
            skLineSegment(sketch, "E161.top", {"start": v(-4.93, -82.82) * mm, "end": v(4.95, -82.82) * mm});
            skLineSegment(sketch, "E161.left", {"start": v(-4.93, -71.14) * mm, "end": v(-4.93, -82.82) * mm});
            skLineSegment(sketch, "E161.right", {"start": v(4.95, -71.14) * mm, "end": v(4.95, -82.82) * mm});
            skPoint(sketch, "E162.oppositeSnap0", {"position": v(-9.18, -87.4) * mm});
            skLineSegment(sketch, "E162.bottom", {"start": v(-4.93, -74.26) * mm, "end": v(-9.18, -74.26) * mm});
            skLineSegment(sketch, "E162.top", {"start": v(-4.93, -79.5) * mm, "end": v(-9.18, -79.5) * mm});
            skLineSegment(sketch, "E162.left", {"start": v(-4.93, -74.26) * mm, "end": v(-4.93, -79.5) * mm});
            skLineSegment(sketch, "E162.right", {"start": v(-9.18, -74.26) * mm, "end": v(-9.18, -79.5) * mm});
            skLineSegment(sketch, "E163.bottom", {"start": v(161.92, -71.14) * mm, "end": v(171.47, -71.14) * mm});
            skLineSegment(sketch, "E163.top", {"start": v(161.92, -82.82) * mm, "end": v(171.47, -82.82) * mm});
            skLineSegment(sketch, "E163.left", {"start": v(161.92, -71.14) * mm, "end": v(161.92, -82.82) * mm});
            skLineSegment(sketch, "E163.right", {"start": v(171.47, -71.14) * mm, "end": v(171.47, -82.82) * mm});
            skPoint(sketch, "E164.oppositeSnap0", {"position": v(175.77, -87.4) * mm});
            skLineSegment(sketch, "E164.bottom", {"start": v(171.47, -74.32) * mm, "end": v(175.77, -74.32) * mm});
            skLineSegment(sketch, "E164.top", {"start": v(171.47, -79.66) * mm, "end": v(175.77, -79.66) * mm});
            skLineSegment(sketch, "E164.left", {"start": v(171.47, -74.32) * mm, "end": v(171.47, -79.66) * mm});
            skLineSegment(sketch, "E164.right", {"start": v(175.77, -74.32) * mm, "end": v(175.77, -79.66) * mm});
            skPoint(sketch, "E165.oppositeSnap0", {"position": v(156.21, -71.14) * mm});
            skLineSegment(sketch, "E165.bottom", {"start": v(161.92, -76.98) * mm, "end": v(156.21, -76.98) * mm});
            skLineSegment(sketch, "E165.top", {"start": v(161.92, -67.72) * mm, "end": v(156.21, -67.72) * mm});
            skLineSegment(sketch, "E165.left", {"start": v(161.92, -76.98) * mm, "end": v(161.92, -67.72) * mm});
            skLineSegment(sketch, "E165.right", {"start": v(156.21, -76.98) * mm, "end": v(156.21, -67.72) * mm});
            skLineSegment(sketch, "E166.bottom", {"start": v(156.21, -76.98) * mm, "end": v(161.92, -76.98) * mm});
            skLineSegment(sketch, "E166.top", {"start": v(156.21, -87.57) * mm, "end": v(161.92, -87.57) * mm});
            skLineSegment(sketch, "E166.left", {"start": v(156.21, -76.98) * mm, "end": v(156.21, -87.57) * mm});
            skLineSegment(sketch, "E166.right", {"start": v(161.92, -76.98) * mm, "end": v(161.92, -87.57) * mm});
            skPoint(sketch, "E167.firstSnap0", {"position": v(124.97, -75.7) * mm});
            skPoint(sketch, "E167.oppositeSnap0", {"position": v(145.8, -78.25) * mm});
            skLineSegment(sketch, "E167.bottom", {"start": v(124.97, -71.14) * mm, "end": v(145.8, -71.14) * mm});
            skLineSegment(sketch, "E167.top", {"start": v(124.97, -82.82) * mm, "end": v(145.8, -82.82) * mm});
            skLineSegment(sketch, "E167.left", {"start": v(124.97, -71.14) * mm, "end": v(124.97, -82.82) * mm});
            skLineSegment(sketch, "E167.right", {"start": v(145.8, -71.14) * mm, "end": v(145.8, -82.82) * mm});
            skPoint(sketch, "E168.firstSnap0", {"position": v(83.31, -75.7) * mm});
            skPoint(sketch, "E168.oppositeSnap0", {"position": v(104.14, -78.25) * mm});
            skLineSegment(sketch, "E168.bottom", {"start": v(83.31, -71.14) * mm, "end": v(104.14, -71.14) * mm});
            skLineSegment(sketch, "E168.top", {"start": v(83.31, -82.82) * mm, "end": v(104.14, -82.82) * mm});
            skLineSegment(sketch, "E168.left", {"start": v(83.31, -71.14) * mm, "end": v(83.31, -82.82) * mm});
            skLineSegment(sketch, "E168.right", {"start": v(104.14, -71.14) * mm, "end": v(104.14, -82.82) * mm});
            skPoint(sketch, "E169.firstSnap0", {"position": v(41.66, -75.7) * mm});
            skPoint(sketch, "E169.oppositeSnap0", {"position": v(62.48, -78.25) * mm});
            skLineSegment(sketch, "E169.bottom", {"start": v(41.66, -71.14) * mm, "end": v(62.48, -71.14) * mm});
            skLineSegment(sketch, "E169.top", {"start": v(41.66, -82.82) * mm, "end": v(62.48, -82.82) * mm});
            skLineSegment(sketch, "E169.left", {"start": v(41.66, -71.14) * mm, "end": v(41.66, -82.82) * mm});
            skLineSegment(sketch, "E169.right", {"start": v(62.48, -71.14) * mm, "end": v(62.48, -82.82) * mm});
            skPoint(sketch, "E170.oppositeSnap0", {"position": v(20.83, -78.25) * mm});
            skLineSegment(sketch, "E170.bottom", {"start": v(4.95, -71.14) * mm, "end": v(20.83, -71.14) * mm});
            skLineSegment(sketch, "E170.top", {"start": v(4.95, -82.82) * mm, "end": v(20.83, -82.82) * mm});
            skLineSegment(sketch, "E170.right", {"start": v(20.83, -71.14) * mm, "end": v(20.83, -82.82) * mm});
            skSolve(sketch);
        }
        {
            var Q0;
            Q0 = qSketchRegion(id + "F20", true);
            extrude(context, id + "F21", {"entities" : qUnion([Q0]), "operationType" : NewBodyOperationType.REMOVE, "oppositeDirection" : true, "depth" : 16.5 * mm, "offsetDistance" : 25.4 * mm});
        }
        {
            var Q0;
            Q0=makeQuery(id+"F4.opExtrude","CAP_FACE",FACE,{"disambiguationData":[OSD([sQuery(id+"F0.wireOp",EDGE,"E20"),sQuery(id+"F0.wireOp",EDGE,"E21.1.0.0"),sQuery(id+"F0.wireOp",EDGE,"E21.2.0.0"),sQuery(id+"F0.wireOp",EDGE,"E21.3.0.0"),sQuery(id+"F0.wireOp",EDGE,"E21.4.0.0"),sQuery(id+"F0.wireOp",EDGE,"E21.5.0.0"),sQuery(id+"F0.wireOp",EDGE,"E22"),sQuery(id+"F0.wireOp",EDGE,"E23.1.0.0"),sQuery(id+"F0.wireOp",EDGE,"E23.2.0.0"),sQuery(id+"F0.wireOp",EDGE,"E23.3.0.0"),sQuery(id+"F0.wireOp",EDGE,"E23.4.0.0"),sQuery(id+"F0.wireOp",EDGE,"E23.5.0.0"),sQuery(id+"F0.wireOp",EDGE,"E24.0.6.0"),sQuery(id+"F0.wireOp",EDGE,"E24.0.7.0"),sQuery(id+"F0.wireOp",EDGE,"E24.0.8.0"),sQuery(id+"F0.wireOp",EDGE,"E25.0.6.0"),sQuery(id+"F0.wireOp",EDGE,"E25.0.7.0"),sQuery(id+"F0.wireOp",EDGE,"E25.0.8.0"),sQuery(id+"F0.wireOp",EDGE,"E26.bottom"),sQuery(id+"F0.wireOp",EDGE,"E26.top"),sQuery(id+"F0.wireOp",EDGE,"E26.left"),sQuery(id+"F0.wireOp",EDGE,"E26.right"),sQuery(id+"F0.wireOp",EDGE,"E41"),sQuery(id+"F0.wireOp",EDGE,"E42"),sQuery(id+"F0.wireOp",EDGE,"E62"),sQuery(id+"F0.wireOp",EDGE,"E63.MirrorC"),sQuery(id+"F0.wireOp",EDGE,"E64.MirrorC"),sQuery(id+"F0.wireOp",EDGE,"E65.MirrorC"),sQuery(id+"F0.wireOp",EDGE,"E73"),sQuery(id+"F0.wireOp",EDGE,"E74"),sQuery(id+"F0.wireOp",EDGE,"E75.MirrorC"),sQuery(id+"F0.wireOp",EDGE,"E76.MirrorC"),sQuery(id+"F0.wireOp",EDGE,"E78.MirrorC"),sQuery(id+"F0.wireOp",EDGE,"E79.MirrorC"),sQuery(id+"F0.wireOp",EDGE,"E80.MirrorC"),sQuery(id+"F0.wireOp",EDGE,"E81.MirrorC"),sQuery(id+"F0.wireOp",EDGE,"E82.2.0.0"),sQuery(id+"F0.wireOp",EDGE,"E82.2.0.1"),sQuery(id+"F0.wireOp",EDGE,"E82.2.0.2"),sQuery(id+"F0.wireOp",EDGE,"E82.2.0.3"),sQuery(id+"F0.wireOp",EDGE,"E82.2.0.4"),sQuery(id+"F0.wireOp",EDGE,"E82.2.0.5"),sQuery(id+"F0.wireOp",EDGE,"E82.2.0.6"),sQuery(id+"F0.wireOp",EDGE,"E82.2.0.7"),sQuery(id+"F0.wireOp",EDGE,"E82.4.0.0"),sQuery(id+"F0.wireOp",EDGE,"E82.4.0.1"),sQuery(id+"F0.wireOp",EDGE,"E82.4.0.2"),sQuery(id+"F0.wireOp",EDGE,"E82.4.0.3"),sQuery(id+"F0.wireOp",EDGE,"E82.4.0.4"),sQuery(id+"F0.wireOp",EDGE,"E82.4.0.5"),sQuery(id+"F0.wireOp",EDGE,"E82.4.0.6"),sQuery(id+"F0.wireOp",EDGE,"E82.4.0.7"),sQuery(id+"F0.wireOp",EDGE,"E82.6.0.0"),sQuery(id+"F0.wireOp",EDGE,"E82.6.0.1"),sQuery(id+"F0.wireOp",EDGE,"E82.6.0.2"),sQuery(id+"F0.wireOp",EDGE,"E82.6.0.3"),sQuery(id+"F0.wireOp",EDGE,"E82.6.0.4"),sQuery(id+"F0.wireOp",EDGE,"E82.6.0.5"),sQuery(id+"F0.wireOp",EDGE,"E82.6.0.6"),sQuery(id+"F0.wireOp",EDGE,"E82.6.0.7"),sQuery(id+"F0.wireOp",EDGE,"E82.7.0.0"),sQuery(id+"F0.wireOp",EDGE,"E82.7.0.2"),sQuery(id+"F0.wireOp",EDGE,"E82.7.0.5"),sQuery(id+"F0.wireOp",EDGE,"E82.7.0.7")])],"isStart":false});
            var sketch = newSketch(context, id + "F22", { "sketchPlane" : qUnion([Q0])});
            skCircle(sketch, "E171", {"center": v(0, -194.4) * mm, "radius": 6.6 * mm});
            skPoint(sketch, "E171.first.point", {"position": v(-4.15, -189.25) * mm});
            skPoint(sketch, "E171.second.point", {"position": v(6.57, -193.7) * mm});
            skPoint(sketch, "E171.third.point", {"position": v(0, -201) * mm});
            skCircle(sketch, "E172", {"center": v(0, -215.22) * mm, "radius": 6.6 * mm});
            skPoint(sketch, "E172.first.point", {"position": v(-4.88, -210.77) * mm});
            skPoint(sketch, "E172.second.point", {"position": v(6.3, -213.24) * mm});
            skPoint(sketch, "E172.third.point", {"position": v(1.78, -221.58) * mm});
            skCircle(sketch, "E173.1.0.0", {"center": v(20.83, -194.4) * mm, "radius": 6.6 * mm});
            skCircle(sketch, "E173.1.0.1", {"center": v(20.83, -215.22) * mm, "radius": 6.6 * mm});
            skCircle(sketch, "E173.2.0.0", {"center": v(41.66, -194.4) * mm, "radius": 6.6 * mm});
            skCircle(sketch, "E173.2.0.1", {"center": v(41.66, -215.22) * mm, "radius": 6.6 * mm});
            skCircle(sketch, "E173.3.0.0", {"center": v(62.48, -194.4) * mm, "radius": 6.6 * mm});
            skCircle(sketch, "E173.3.0.1", {"center": v(62.48, -215.22) * mm, "radius": 6.6 * mm});
            skCircle(sketch, "E173.4.0.0", {"center": v(83.31, -194.4) * mm, "radius": 6.6 * mm});
            skCircle(sketch, "E173.4.0.1", {"center": v(83.31, -215.22) * mm, "radius": 6.6 * mm});
            skCircle(sketch, "E173.5.0.0", {"center": v(104.14, -194.4) * mm, "radius": 6.6 * mm});
            skCircle(sketch, "E173.5.0.1", {"center": v(104.14, -215.22) * mm, "radius": 6.6 * mm});
            skCircle(sketch, "E173.6.0.0", {"center": v(124.97, -194.4) * mm, "radius": 6.6 * mm});
            skCircle(sketch, "E173.6.0.1", {"center": v(124.97, -215.22) * mm, "radius": 6.6 * mm});
            skCircle(sketch, "E173.7.0.0", {"center": v(145.8, -194.4) * mm, "radius": 6.6 * mm});
            skCircle(sketch, "E173.7.0.1", {"center": v(145.8, -215.22) * mm, "radius": 6.6 * mm});
            skCircle(sketch, "E173.8.0.0", {"center": v(166.62, -194.4) * mm, "radius": 6.6 * mm});
            skCircle(sketch, "E173.8.0.1", {"center": v(166.62, -215.22) * mm, "radius": 6.6 * mm});
            skLineSegment(sketch, "E173.direction1", {"start": v(0, -194.4) * mm, "end": v(20.83, -194.4) * mm, "construction": true});
            skSolve(sketch);
        }
        {
            var Q0;
            Q0 = qSketchRegion(id + "F22", true);
            extrude(context, id + "F23", {"entities" : qUnion([Q0]), "operationType" : NewBodyOperationType.ADD, "oppositeDirection" : true, "depth" : 2.54 * mm, "offsetDistance" : 25.4 * mm});
        }
        {
            var Q0;
            Q0=makeQuery(id+"F2.opExtrude","CAP_FACE",FACE,{"disambiguationData":[OSD([sQuery(id+"F0.wireOp",EDGE,"E6"),sQuery(id+"F0.wireOp",EDGE,"E7.1.0.0"),sQuery(id+"F0.wireOp",EDGE,"E7.2.0.0"),sQuery(id+"F0.wireOp",EDGE,"E7.3.0.0"),sQuery(id+"F0.wireOp",EDGE,"E7.4.0.0"),sQuery(id+"F0.wireOp",EDGE,"E7.5.0.0"),sQuery(id+"F0.wireOp",EDGE,"E8"),sQuery(id+"F0.wireOp",EDGE,"E9.1.0.0"),sQuery(id+"F0.wireOp",EDGE,"E9.2.0.0"),sQuery(id+"F0.wireOp",EDGE,"E9.3.0.0"),sQuery(id+"F0.wireOp",EDGE,"E9.4.0.0"),sQuery(id+"F0.wireOp",EDGE,"E9.5.0.0"),sQuery(id+"F0.wireOp",EDGE,"E10.0.6.0"),sQuery(id+"F0.wireOp",EDGE,"E10.0.7.0"),sQuery(id+"F0.wireOp",EDGE,"E10.0.8.0"),sQuery(id+"F0.wireOp",EDGE,"E11.0.6.0"),sQuery(id+"F0.wireOp",EDGE,"E11.0.7.0"),sQuery(id+"F0.wireOp",EDGE,"E11.0.8.0"),sQuery(id+"F0.wireOp",EDGE,"E12.bottom"),sQuery(id+"F0.wireOp",EDGE,"E12.top"),sQuery(id+"F0.wireOp",EDGE,"E12.left"),sQuery(id+"F0.wireOp",EDGE,"E12.right"),sQuery(id+"F0.wireOp",EDGE,"E108"),sQuery(id+"F0.wireOp",EDGE,"E109"),sQuery(id+"F0.wireOp",EDGE,"E110"),sQuery(id+"F0.wireOp",EDGE,"E111")])],"isStart":true});
            var sketch = newSketch(context, id + "F24", { "sketchPlane" : qUnion([Q0])});
            skCircle(sketch, "E174", {"center": v(0, 87.4) * mm, "radius": 6.6 * mm});
            skPoint(sketch, "E174.first.point", {"position": v(-3.8, 92.79) * mm});
            skPoint(sketch, "E174.second.point", {"position": v(6.09, 89.95) * mm});
            skPoint(sketch, "E174.third.point", {"position": v(4.64, 82.69) * mm});
            skCircle(sketch, "E175", {"center": v(0, 66.56) * mm, "radius": 6.6 * mm});
            skPoint(sketch, "E175.first.point", {"position": v(-4.55, 71.35) * mm});
            skPoint(sketch, "E175.second.point", {"position": v(6.47, 67.89) * mm});
            skPoint(sketch, "E175.third.point", {"position": v(-1.22, 60.07) * mm});
            skCircle(sketch, "E176.1.0.0", {"center": v(20.83, 87.4) * mm, "radius": 6.6 * mm});
            skCircle(sketch, "E176.1.0.1", {"center": v(20.83, 66.56) * mm, "radius": 6.6 * mm});
            skCircle(sketch, "E176.2.0.0", {"center": v(41.66, 87.4) * mm, "radius": 6.6 * mm});
            skCircle(sketch, "E176.2.0.1", {"center": v(41.66, 66.56) * mm, "radius": 6.6 * mm});
            skCircle(sketch, "E176.3.0.0", {"center": v(62.48, 87.4) * mm, "radius": 6.6 * mm});
            skCircle(sketch, "E176.3.0.1", {"center": v(62.48, 66.56) * mm, "radius": 6.6 * mm});
            skCircle(sketch, "E176.4.0.0", {"center": v(83.31, 87.4) * mm, "radius": 6.6 * mm});
            skCircle(sketch, "E176.4.0.1", {"center": v(83.31, 66.56) * mm, "radius": 6.6 * mm});
            skCircle(sketch, "E176.5.0.0", {"center": v(104.14, 87.4) * mm, "radius": 6.6 * mm});
            skCircle(sketch, "E176.5.0.1", {"center": v(104.14, 66.56) * mm, "radius": 6.6 * mm});
            skCircle(sketch, "E176.6.0.0", {"center": v(124.97, 87.4) * mm, "radius": 6.6 * mm});
            skCircle(sketch, "E176.6.0.1", {"center": v(124.97, 66.56) * mm, "radius": 6.6 * mm});
            skCircle(sketch, "E176.7.0.0", {"center": v(145.8, 87.4) * mm, "radius": 6.6 * mm});
            skCircle(sketch, "E176.7.0.1", {"center": v(145.8, 66.56) * mm, "radius": 6.6 * mm});
            skCircle(sketch, "E176.8.0.0", {"center": v(166.62, 87.4) * mm, "radius": 6.6 * mm});
            skCircle(sketch, "E176.8.0.1", {"center": v(166.62, 66.56) * mm, "radius": 6.6 * mm});
            skLineSegment(sketch, "E176.direction1", {"start": v(0, 87.4) * mm, "end": v(20.83, 87.4) * mm, "construction": true});
            skSolve(sketch);
        }
        {
            var Q0;
            Q0 = qSketchRegion(id + "F24", true);
            extrude(context, id + "F25", {"entities" : qUnion([Q0]), "operationType" : NewBodyOperationType.ADD, "oppositeDirection" : true, "depth" : 2.54 * mm, "offsetDistance" : 25.4 * mm});
        }
        {
            var Q0;
            Q0=makeQuery(id+"F4.opExtrude","SWEPT_BODY",BODY,{"disambiguationData":[OSD([sQuery(id+"F0.wireOp",EDGE,"E20"),sQuery(id+"F0.wireOp",EDGE,"E21.1.0.0"),sQuery(id+"F0.wireOp",EDGE,"E21.2.0.0"),sQuery(id+"F0.wireOp",EDGE,"E21.3.0.0"),sQuery(id+"F0.wireOp",EDGE,"E21.4.0.0"),sQuery(id+"F0.wireOp",EDGE,"E21.5.0.0"),sQuery(id+"F0.wireOp",EDGE,"E22"),sQuery(id+"F0.wireOp",EDGE,"E23.1.0.0"),sQuery(id+"F0.wireOp",EDGE,"E23.2.0.0"),sQuery(id+"F0.wireOp",EDGE,"E23.3.0.0"),sQuery(id+"F0.wireOp",EDGE,"E23.4.0.0"),sQuery(id+"F0.wireOp",EDGE,"E23.5.0.0"),sQuery(id+"F0.wireOp",EDGE,"E24.0.6.0"),sQuery(id+"F0.wireOp",EDGE,"E24.0.7.0"),sQuery(id+"F0.wireOp",EDGE,"E24.0.8.0"),sQuery(id+"F0.wireOp",EDGE,"E25.0.6.0"),sQuery(id+"F0.wireOp",EDGE,"E25.0.7.0"),sQuery(id+"F0.wireOp",EDGE,"E25.0.8.0"),sQuery(id+"F0.wireOp",EDGE,"E26.bottom"),sQuery(id+"F0.wireOp",EDGE,"E26.top"),sQuery(id+"F0.wireOp",EDGE,"E26.left"),sQuery(id+"F0.wireOp",EDGE,"E26.right"),sQuery(id+"F0.wireOp",EDGE,"E41"),sQuery(id+"F0.wireOp",EDGE,"E42"),sQuery(id+"F0.wireOp",EDGE,"E62"),sQuery(id+"F0.wireOp",EDGE,"E63.MirrorC"),sQuery(id+"F0.wireOp",EDGE,"E64.MirrorC"),sQuery(id+"F0.wireOp",EDGE,"E65.MirrorC"),sQuery(id+"F0.wireOp",EDGE,"E73"),sQuery(id+"F0.wireOp",EDGE,"E74"),sQuery(id+"F0.wireOp",EDGE,"E75.MirrorC"),sQuery(id+"F0.wireOp",EDGE,"E76.MirrorC"),sQuery(id+"F0.wireOp",EDGE,"E78.MirrorC"),sQuery(id+"F0.wireOp",EDGE,"E79.MirrorC"),sQuery(id+"F0.wireOp",EDGE,"E80.MirrorC"),sQuery(id+"F0.wireOp",EDGE,"E81.MirrorC"),sQuery(id+"F0.wireOp",EDGE,"E82.2.0.0"),sQuery(id+"F0.wireOp",EDGE,"E82.2.0.1"),sQuery(id+"F0.wireOp",EDGE,"E82.2.0.2"),sQuery(id+"F0.wireOp",EDGE,"E82.2.0.3"),sQuery(id+"F0.wireOp",EDGE,"E82.2.0.4"),sQuery(id+"F0.wireOp",EDGE,"E82.2.0.5"),sQuery(id+"F0.wireOp",EDGE,"E82.2.0.6"),sQuery(id+"F0.wireOp",EDGE,"E82.2.0.7"),sQuery(id+"F0.wireOp",EDGE,"E82.4.0.0"),sQuery(id+"F0.wireOp",EDGE,"E82.4.0.1"),sQuery(id+"F0.wireOp",EDGE,"E82.4.0.2"),sQuery(id+"F0.wireOp",EDGE,"E82.4.0.3"),sQuery(id+"F0.wireOp",EDGE,"E82.4.0.4"),sQuery(id+"F0.wireOp",EDGE,"E82.4.0.5"),sQuery(id+"F0.wireOp",EDGE,"E82.4.0.6"),sQuery(id+"F0.wireOp",EDGE,"E82.4.0.7"),sQuery(id+"F0.wireOp",EDGE,"E82.6.0.0"),sQuery(id+"F0.wireOp",EDGE,"E82.6.0.1"),sQuery(id+"F0.wireOp",EDGE,"E82.6.0.2"),sQuery(id+"F0.wireOp",EDGE,"E82.6.0.3"),sQuery(id+"F0.wireOp",EDGE,"E82.6.0.4"),sQuery(id+"F0.wireOp",EDGE,"E82.6.0.5"),sQuery(id+"F0.wireOp",EDGE,"E82.6.0.6"),sQuery(id+"F0.wireOp",EDGE,"E82.6.0.7"),sQuery(id+"F0.wireOp",EDGE,"E82.7.0.0"),sQuery(id+"F0.wireOp",EDGE,"E82.7.0.2"),sQuery(id+"F0.wireOp",EDGE,"E82.7.0.5"),sQuery(id+"F0.wireOp",EDGE,"E82.7.0.7")])]});
            transform(context, id + "F26", {"entities" : qUnion([Q0]), "transformType" : TransformType.TRANSLATION_3D, "dx" : 0 * mm, "dy" : 127.84 * mm, "dz" : 44.96 * mm, "makeCopy" : false});
        }
        {
            var Q0;
            Q0=makeQuery(id+"F3.opExtrude","SWEPT_BODY",BODY,{"disambiguationData":[OSD([sQuery(id+"F0.wireOp",EDGE,"E13"),sQuery(id+"F0.wireOp",EDGE,"E14.1.0.0"),sQuery(id+"F0.wireOp",EDGE,"E14.2.0.0"),sQuery(id+"F0.wireOp",EDGE,"E14.3.0.0"),sQuery(id+"F0.wireOp",EDGE,"E14.4.0.0"),sQuery(id+"F0.wireOp",EDGE,"E14.5.0.0"),sQuery(id+"F0.wireOp",EDGE,"E15"),sQuery(id+"F0.wireOp",EDGE,"E16.1.0.0"),sQuery(id+"F0.wireOp",EDGE,"E16.2.0.0"),sQuery(id+"F0.wireOp",EDGE,"E16.3.0.0"),sQuery(id+"F0.wireOp",EDGE,"E16.4.0.0"),sQuery(id+"F0.wireOp",EDGE,"E16.5.0.0"),sQuery(id+"F0.wireOp",EDGE,"E17.0.6.0"),sQuery(id+"F0.wireOp",EDGE,"E17.0.7.0"),sQuery(id+"F0.wireOp",EDGE,"E17.0.8.0"),sQuery(id+"F0.wireOp",EDGE,"E18.0.6.0"),sQuery(id+"F0.wireOp",EDGE,"E18.0.7.0"),sQuery(id+"F0.wireOp",EDGE,"E18.0.8.0"),sQuery(id+"F0.wireOp",EDGE,"E19.bottom"),sQuery(id+"F0.wireOp",EDGE,"E19.top"),sQuery(id+"F0.wireOp",EDGE,"E19.left"),sQuery(id+"F0.wireOp",EDGE,"E19.right"),sQuery(id+"F0.wireOp",EDGE,"E36"),sQuery(id+"F0.wireOp",EDGE,"E38"),sQuery(id+"F0.wireOp",EDGE,"E69.MirrorC"),sQuery(id+"F0.wireOp",EDGE,"E70.MirrorC"),sQuery(id+"F0.wireOp",EDGE,"E71.MirrorC"),sQuery(id+"F0.wireOp",EDGE,"E72.MirrorC"),sQuery(id+"F0.wireOp",EDGE,"E83.MirrorC"),sQuery(id+"F0.wireOp",EDGE,"E84.MirrorC"),sQuery(id+"F0.wireOp",EDGE,"E85.MirrorC"),sQuery(id+"F0.wireOp",EDGE,"E86.MirrorC"),sQuery(id+"F0.wireOp",EDGE,"E87.MirrorC"),sQuery(id+"F0.wireOp",EDGE,"E88.MirrorC"),sQuery(id+"F0.wireOp",EDGE,"E89.MirrorC"),sQuery(id+"F0.wireOp",EDGE,"E90.MirrorC"),sQuery(id+"F0.wireOp",EDGE,"E91.MirrorC"),sQuery(id+"F0.wireOp",EDGE,"E92.MirrorC"),sQuery(id+"F0.wireOp",EDGE,"E93.MirrorC"),sQuery(id+"F0.wireOp",EDGE,"E94.MirrorC"),sQuery(id+"F0.wireOp",EDGE,"E96.MirrorC"),sQuery(id+"F0.wireOp",EDGE,"E97.MirrorC"),sQuery(id+"F0.wireOp",EDGE,"E98.MirrorC"),sQuery(id+"F0.wireOp",EDGE,"E99.MirrorC"),sQuery(id+"F0.wireOp",EDGE,"E95.MirrorC"),sQuery(id+"F0.wireOp",EDGE,"E100.MirrorC")])]});
            transform(context, id + "F27", {"entities" : qUnion([Q0]), "transformType" : TransformType.TRANSLATION_3D, "dx" : 0 * mm, "dy" : 61.1 * mm, "dz" : 22.73 * mm, "makeCopy" : false});
        }
        {
            var Q0;
            Q0=makeQuery(id+"F2.opExtrude","SWEPT_BODY",BODY,{"disambiguationData":[OSD([sQuery(id+"F0.wireOp",EDGE,"E6"),sQuery(id+"F0.wireOp",EDGE,"E7.1.0.0"),sQuery(id+"F0.wireOp",EDGE,"E7.2.0.0"),sQuery(id+"F0.wireOp",EDGE,"E7.3.0.0"),sQuery(id+"F0.wireOp",EDGE,"E7.4.0.0"),sQuery(id+"F0.wireOp",EDGE,"E7.5.0.0"),sQuery(id+"F0.wireOp",EDGE,"E8"),sQuery(id+"F0.wireOp",EDGE,"E9.1.0.0"),sQuery(id+"F0.wireOp",EDGE,"E9.2.0.0"),sQuery(id+"F0.wireOp",EDGE,"E9.3.0.0"),sQuery(id+"F0.wireOp",EDGE,"E9.4.0.0"),sQuery(id+"F0.wireOp",EDGE,"E9.5.0.0"),sQuery(id+"F0.wireOp",EDGE,"E10.0.6.0"),sQuery(id+"F0.wireOp",EDGE,"E10.0.7.0"),sQuery(id+"F0.wireOp",EDGE,"E10.0.8.0"),sQuery(id+"F0.wireOp",EDGE,"E11.0.6.0"),sQuery(id+"F0.wireOp",EDGE,"E11.0.7.0"),sQuery(id+"F0.wireOp",EDGE,"E11.0.8.0"),sQuery(id+"F0.wireOp",EDGE,"E12.bottom"),sQuery(id+"F0.wireOp",EDGE,"E12.top"),sQuery(id+"F0.wireOp",EDGE,"E12.left"),sQuery(id+"F0.wireOp",EDGE,"E12.right"),sQuery(id+"F0.wireOp",EDGE,"E108"),sQuery(id+"F0.wireOp",EDGE,"E109"),sQuery(id+"F0.wireOp",EDGE,"E110"),sQuery(id+"F0.wireOp",EDGE,"E111")])]});
            transform(context, id + "F28", {"entities" : qUnion([Q0]), "transformType" : TransformType.TRANSLATION_3D, "dx" : 0 * mm, "dy" : 0 * mm, "dz" : -8.9 * mm, "makeCopy" : false});
        }
        {
            var Q0;
            Q0=makeQuery(id+"F2.opExtrude","SWEPT_BODY",BODY,{"disambiguationData":[OSD([sQuery(id+"F0.wireOp",EDGE,"E6"),sQuery(id+"F0.wireOp",EDGE,"E7.1.0.0"),sQuery(id+"F0.wireOp",EDGE,"E7.2.0.0"),sQuery(id+"F0.wireOp",EDGE,"E7.3.0.0"),sQuery(id+"F0.wireOp",EDGE,"E7.4.0.0"),sQuery(id+"F0.wireOp",EDGE,"E7.5.0.0"),sQuery(id+"F0.wireOp",EDGE,"E8"),sQuery(id+"F0.wireOp",EDGE,"E9.1.0.0"),sQuery(id+"F0.wireOp",EDGE,"E9.2.0.0"),sQuery(id+"F0.wireOp",EDGE,"E9.3.0.0"),sQuery(id+"F0.wireOp",EDGE,"E9.4.0.0"),sQuery(id+"F0.wireOp",EDGE,"E9.5.0.0"),sQuery(id+"F0.wireOp",EDGE,"E10.0.6.0"),sQuery(id+"F0.wireOp",EDGE,"E10.0.7.0"),sQuery(id+"F0.wireOp",EDGE,"E10.0.8.0"),sQuery(id+"F0.wireOp",EDGE,"E11.0.6.0"),sQuery(id+"F0.wireOp",EDGE,"E11.0.7.0"),sQuery(id+"F0.wireOp",EDGE,"E11.0.8.0"),sQuery(id+"F0.wireOp",EDGE,"E12.bottom"),sQuery(id+"F0.wireOp",EDGE,"E12.top"),sQuery(id+"F0.wireOp",EDGE,"E12.left"),sQuery(id+"F0.wireOp",EDGE,"E12.right"),sQuery(id+"F0.wireOp",EDGE,"E108"),sQuery(id+"F0.wireOp",EDGE,"E109"),sQuery(id+"F0.wireOp",EDGE,"E110"),sQuery(id+"F0.wireOp",EDGE,"E111")])]});
            var Q1;
            Q1=makeQuery(id+"F3.opExtrude","SWEPT_BODY",BODY,{"disambiguationData":[OSD([sQuery(id+"F0.wireOp",EDGE,"E13"),sQuery(id+"F0.wireOp",EDGE,"E14.1.0.0"),sQuery(id+"F0.wireOp",EDGE,"E14.2.0.0"),sQuery(id+"F0.wireOp",EDGE,"E14.3.0.0"),sQuery(id+"F0.wireOp",EDGE,"E14.4.0.0"),sQuery(id+"F0.wireOp",EDGE,"E14.5.0.0"),sQuery(id+"F0.wireOp",EDGE,"E15"),sQuery(id+"F0.wireOp",EDGE,"E16.1.0.0"),sQuery(id+"F0.wireOp",EDGE,"E16.2.0.0"),sQuery(id+"F0.wireOp",EDGE,"E16.3.0.0"),sQuery(id+"F0.wireOp",EDGE,"E16.4.0.0"),sQuery(id+"F0.wireOp",EDGE,"E16.5.0.0"),sQuery(id+"F0.wireOp",EDGE,"E17.0.6.0"),sQuery(id+"F0.wireOp",EDGE,"E17.0.7.0"),sQuery(id+"F0.wireOp",EDGE,"E17.0.8.0"),sQuery(id+"F0.wireOp",EDGE,"E18.0.6.0"),sQuery(id+"F0.wireOp",EDGE,"E18.0.7.0"),sQuery(id+"F0.wireOp",EDGE,"E18.0.8.0"),sQuery(id+"F0.wireOp",EDGE,"E19.bottom"),sQuery(id+"F0.wireOp",EDGE,"E19.top"),sQuery(id+"F0.wireOp",EDGE,"E19.left"),sQuery(id+"F0.wireOp",EDGE,"E19.right"),sQuery(id+"F0.wireOp",EDGE,"E36"),sQuery(id+"F0.wireOp",EDGE,"E38"),sQuery(id+"F0.wireOp",EDGE,"E69.MirrorC"),sQuery(id+"F0.wireOp",EDGE,"E70.MirrorC"),sQuery(id+"F0.wireOp",EDGE,"E71.MirrorC"),sQuery(id+"F0.wireOp",EDGE,"E72.MirrorC"),sQuery(id+"F0.wireOp",EDGE,"E83.MirrorC"),sQuery(id+"F0.wireOp",EDGE,"E84.MirrorC"),sQuery(id+"F0.wireOp",EDGE,"E85.MirrorC"),sQuery(id+"F0.wireOp",EDGE,"E86.MirrorC"),sQuery(id+"F0.wireOp",EDGE,"E87.MirrorC"),sQuery(id+"F0.wireOp",EDGE,"E88.MirrorC"),sQuery(id+"F0.wireOp",EDGE,"E89.MirrorC"),sQuery(id+"F0.wireOp",EDGE,"E90.MirrorC"),sQuery(id+"F0.wireOp",EDGE,"E91.MirrorC"),sQuery(id+"F0.wireOp",EDGE,"E92.MirrorC"),sQuery(id+"F0.wireOp",EDGE,"E93.MirrorC"),sQuery(id+"F0.wireOp",EDGE,"E94.MirrorC"),sQuery(id+"F0.wireOp",EDGE,"E96.MirrorC"),sQuery(id+"F0.wireOp",EDGE,"E97.MirrorC"),sQuery(id+"F0.wireOp",EDGE,"E98.MirrorC"),sQuery(id+"F0.wireOp",EDGE,"E99.MirrorC"),sQuery(id+"F0.wireOp",EDGE,"E95.MirrorC"),sQuery(id+"F0.wireOp",EDGE,"E100.MirrorC")])]});
            var Q2;
            Q2=makeQuery(id+"F4.opExtrude","SWEPT_BODY",BODY,{"disambiguationData":[OSD([sQuery(id+"F0.wireOp",EDGE,"E20"),sQuery(id+"F0.wireOp",EDGE,"E21.1.0.0"),sQuery(id+"F0.wireOp",EDGE,"E21.2.0.0"),sQuery(id+"F0.wireOp",EDGE,"E21.3.0.0"),sQuery(id+"F0.wireOp",EDGE,"E21.4.0.0"),sQuery(id+"F0.wireOp",EDGE,"E21.5.0.0"),sQuery(id+"F0.wireOp",EDGE,"E22"),sQuery(id+"F0.wireOp",EDGE,"E23.1.0.0"),sQuery(id+"F0.wireOp",EDGE,"E23.2.0.0"),sQuery(id+"F0.wireOp",EDGE,"E23.3.0.0"),sQuery(id+"F0.wireOp",EDGE,"E23.4.0.0"),sQuery(id+"F0.wireOp",EDGE,"E23.5.0.0"),sQuery(id+"F0.wireOp",EDGE,"E24.0.6.0"),sQuery(id+"F0.wireOp",EDGE,"E24.0.7.0"),sQuery(id+"F0.wireOp",EDGE,"E24.0.8.0"),sQuery(id+"F0.wireOp",EDGE,"E25.0.6.0"),sQuery(id+"F0.wireOp",EDGE,"E25.0.7.0"),sQuery(id+"F0.wireOp",EDGE,"E25.0.8.0"),sQuery(id+"F0.wireOp",EDGE,"E26.bottom"),sQuery(id+"F0.wireOp",EDGE,"E26.top"),sQuery(id+"F0.wireOp",EDGE,"E26.left"),sQuery(id+"F0.wireOp",EDGE,"E26.right"),sQuery(id+"F0.wireOp",EDGE,"E41"),sQuery(id+"F0.wireOp",EDGE,"E42"),sQuery(id+"F0.wireOp",EDGE,"E62"),sQuery(id+"F0.wireOp",EDGE,"E63.MirrorC"),sQuery(id+"F0.wireOp",EDGE,"E64.MirrorC"),sQuery(id+"F0.wireOp",EDGE,"E65.MirrorC"),sQuery(id+"F0.wireOp",EDGE,"E73"),sQuery(id+"F0.wireOp",EDGE,"E74"),sQuery(id+"F0.wireOp",EDGE,"E75.MirrorC"),sQuery(id+"F0.wireOp",EDGE,"E76.MirrorC"),sQuery(id+"F0.wireOp",EDGE,"E78.MirrorC"),sQuery(id+"F0.wireOp",EDGE,"E79.MirrorC"),sQuery(id+"F0.wireOp",EDGE,"E80.MirrorC"),sQuery(id+"F0.wireOp",EDGE,"E81.MirrorC"),sQuery(id+"F0.wireOp",EDGE,"E82.2.0.0"),sQuery(id+"F0.wireOp",EDGE,"E82.2.0.1"),sQuery(id+"F0.wireOp",EDGE,"E82.2.0.2"),sQuery(id+"F0.wireOp",EDGE,"E82.2.0.3"),sQuery(id+"F0.wireOp",EDGE,"E82.2.0.4"),sQuery(id+"F0.wireOp",EDGE,"E82.2.0.5"),sQuery(id+"F0.wireOp",EDGE,"E82.2.0.6"),sQuery(id+"F0.wireOp",EDGE,"E82.2.0.7"),sQuery(id+"F0.wireOp",EDGE,"E82.4.0.0"),sQuery(id+"F0.wireOp",EDGE,"E82.4.0.1"),sQuery(id+"F0.wireOp",EDGE,"E82.4.0.2"),sQuery(id+"F0.wireOp",EDGE,"E82.4.0.3"),sQuery(id+"F0.wireOp",EDGE,"E82.4.0.4"),sQuery(id+"F0.wireOp",EDGE,"E82.4.0.5"),sQuery(id+"F0.wireOp",EDGE,"E82.4.0.6"),sQuery(id+"F0.wireOp",EDGE,"E82.4.0.7"),sQuery(id+"F0.wireOp",EDGE,"E82.6.0.0"),sQuery(id+"F0.wireOp",EDGE,"E82.6.0.1"),sQuery(id+"F0.wireOp",EDGE,"E82.6.0.2"),sQuery(id+"F0.wireOp",EDGE,"E82.6.0.3"),sQuery(id+"F0.wireOp",EDGE,"E82.6.0.4"),sQuery(id+"F0.wireOp",EDGE,"E82.6.0.5"),sQuery(id+"F0.wireOp",EDGE,"E82.6.0.6"),sQuery(id+"F0.wireOp",EDGE,"E82.6.0.7"),sQuery(id+"F0.wireOp",EDGE,"E82.7.0.0"),sQuery(id+"F0.wireOp",EDGE,"E82.7.0.2"),sQuery(id+"F0.wireOp",EDGE,"E82.7.0.5"),sQuery(id+"F0.wireOp",EDGE,"E82.7.0.7")])]});
            transform(context, id + "F29", {"entities" : qUnion([Q0, Q1, Q2]), "transformType" : TransformType.TRANSLATION_3D, "dx" : 0 * mm, "dy" : 0 * mm, "dz" : 8.9 * mm, "makeCopy" : false});
        }
        {
            var Q0;
            Q0=makeQuery(id+"F2.opExtrude","SWEPT_BODY",BODY,{"disambiguationData":[OSD([sQuery(id+"F0.wireOp",EDGE,"E6"),sQuery(id+"F0.wireOp",EDGE,"E7.1.0.0"),sQuery(id+"F0.wireOp",EDGE,"E7.2.0.0"),sQuery(id+"F0.wireOp",EDGE,"E7.3.0.0"),sQuery(id+"F0.wireOp",EDGE,"E7.4.0.0"),sQuery(id+"F0.wireOp",EDGE,"E7.5.0.0"),sQuery(id+"F0.wireOp",EDGE,"E8"),sQuery(id+"F0.wireOp",EDGE,"E9.1.0.0"),sQuery(id+"F0.wireOp",EDGE,"E9.2.0.0"),sQuery(id+"F0.wireOp",EDGE,"E9.3.0.0"),sQuery(id+"F0.wireOp",EDGE,"E9.4.0.0"),sQuery(id+"F0.wireOp",EDGE,"E9.5.0.0"),sQuery(id+"F0.wireOp",EDGE,"E10.0.6.0"),sQuery(id+"F0.wireOp",EDGE,"E10.0.7.0"),sQuery(id+"F0.wireOp",EDGE,"E10.0.8.0"),sQuery(id+"F0.wireOp",EDGE,"E11.0.6.0"),sQuery(id+"F0.wireOp",EDGE,"E11.0.7.0"),sQuery(id+"F0.wireOp",EDGE,"E11.0.8.0"),sQuery(id+"F0.wireOp",EDGE,"E12.bottom"),sQuery(id+"F0.wireOp",EDGE,"E12.top"),sQuery(id+"F0.wireOp",EDGE,"E12.left"),sQuery(id+"F0.wireOp",EDGE,"E12.right"),sQuery(id+"F0.wireOp",EDGE,"E108"),sQuery(id+"F0.wireOp",EDGE,"E109"),sQuery(id+"F0.wireOp",EDGE,"E110"),sQuery(id+"F0.wireOp",EDGE,"E111")])]});
            transform(context, id + "F30", {"entities" : qUnion([Q0]), "transformType" : TransformType.TRANSLATION_3D, "dx" : 0 * mm, "dy" : 87.43 * mm, "dz" : 0 * mm, "makeCopy" : false});
        }
        {
            var Q0;
            Q0=makeQuery(id+"F3.opExtrude","SWEPT_BODY",BODY,{"disambiguationData":[OSD([sQuery(id+"F0.wireOp",EDGE,"E13"),sQuery(id+"F0.wireOp",EDGE,"E14.1.0.0"),sQuery(id+"F0.wireOp",EDGE,"E14.2.0.0"),sQuery(id+"F0.wireOp",EDGE,"E14.3.0.0"),sQuery(id+"F0.wireOp",EDGE,"E14.4.0.0"),sQuery(id+"F0.wireOp",EDGE,"E14.5.0.0"),sQuery(id+"F0.wireOp",EDGE,"E15"),sQuery(id+"F0.wireOp",EDGE,"E16.1.0.0"),sQuery(id+"F0.wireOp",EDGE,"E16.2.0.0"),sQuery(id+"F0.wireOp",EDGE,"E16.3.0.0"),sQuery(id+"F0.wireOp",EDGE,"E16.4.0.0"),sQuery(id+"F0.wireOp",EDGE,"E16.5.0.0"),sQuery(id+"F0.wireOp",EDGE,"E17.0.6.0"),sQuery(id+"F0.wireOp",EDGE,"E17.0.7.0"),sQuery(id+"F0.wireOp",EDGE,"E17.0.8.0"),sQuery(id+"F0.wireOp",EDGE,"E18.0.6.0"),sQuery(id+"F0.wireOp",EDGE,"E18.0.7.0"),sQuery(id+"F0.wireOp",EDGE,"E18.0.8.0"),sQuery(id+"F0.wireOp",EDGE,"E19.bottom"),sQuery(id+"F0.wireOp",EDGE,"E19.top"),sQuery(id+"F0.wireOp",EDGE,"E19.left"),sQuery(id+"F0.wireOp",EDGE,"E19.right"),sQuery(id+"F0.wireOp",EDGE,"E36"),sQuery(id+"F0.wireOp",EDGE,"E38"),sQuery(id+"F0.wireOp",EDGE,"E69.MirrorC"),sQuery(id+"F0.wireOp",EDGE,"E70.MirrorC"),sQuery(id+"F0.wireOp",EDGE,"E71.MirrorC"),sQuery(id+"F0.wireOp",EDGE,"E72.MirrorC"),sQuery(id+"F0.wireOp",EDGE,"E83.MirrorC"),sQuery(id+"F0.wireOp",EDGE,"E84.MirrorC"),sQuery(id+"F0.wireOp",EDGE,"E85.MirrorC"),sQuery(id+"F0.wireOp",EDGE,"E86.MirrorC"),sQuery(id+"F0.wireOp",EDGE,"E87.MirrorC"),sQuery(id+"F0.wireOp",EDGE,"E88.MirrorC"),sQuery(id+"F0.wireOp",EDGE,"E89.MirrorC"),sQuery(id+"F0.wireOp",EDGE,"E90.MirrorC"),sQuery(id+"F0.wireOp",EDGE,"E91.MirrorC"),sQuery(id+"F0.wireOp",EDGE,"E92.MirrorC"),sQuery(id+"F0.wireOp",EDGE,"E93.MirrorC"),sQuery(id+"F0.wireOp",EDGE,"E94.MirrorC"),sQuery(id+"F0.wireOp",EDGE,"E96.MirrorC"),sQuery(id+"F0.wireOp",EDGE,"E97.MirrorC"),sQuery(id+"F0.wireOp",EDGE,"E98.MirrorC"),sQuery(id+"F0.wireOp",EDGE,"E99.MirrorC"),sQuery(id+"F0.wireOp",EDGE,"E95.MirrorC"),sQuery(id+"F0.wireOp",EDGE,"E100.MirrorC")])]});
            transform(context, id + "F31", {"entities" : qUnion([Q0]), "transformType" : TransformType.TRANSLATION_3D, "dx" : 0 * mm, "dy" : 87.43 * mm, "dz" : 0 * mm, "makeCopy" : false});
        }
        {
            var Q0;
            Q0=makeQuery(id+"F4.opExtrude","SWEPT_BODY",BODY,{"disambiguationData":[OSD([sQuery(id+"F0.wireOp",EDGE,"E20"),sQuery(id+"F0.wireOp",EDGE,"E21.1.0.0"),sQuery(id+"F0.wireOp",EDGE,"E21.2.0.0"),sQuery(id+"F0.wireOp",EDGE,"E21.3.0.0"),sQuery(id+"F0.wireOp",EDGE,"E21.4.0.0"),sQuery(id+"F0.wireOp",EDGE,"E21.5.0.0"),sQuery(id+"F0.wireOp",EDGE,"E22"),sQuery(id+"F0.wireOp",EDGE,"E23.1.0.0"),sQuery(id+"F0.wireOp",EDGE,"E23.2.0.0"),sQuery(id+"F0.wireOp",EDGE,"E23.3.0.0"),sQuery(id+"F0.wireOp",EDGE,"E23.4.0.0"),sQuery(id+"F0.wireOp",EDGE,"E23.5.0.0"),sQuery(id+"F0.wireOp",EDGE,"E24.0.6.0"),sQuery(id+"F0.wireOp",EDGE,"E24.0.7.0"),sQuery(id+"F0.wireOp",EDGE,"E24.0.8.0"),sQuery(id+"F0.wireOp",EDGE,"E25.0.6.0"),sQuery(id+"F0.wireOp",EDGE,"E25.0.7.0"),sQuery(id+"F0.wireOp",EDGE,"E25.0.8.0"),sQuery(id+"F0.wireOp",EDGE,"E26.bottom"),sQuery(id+"F0.wireOp",EDGE,"E26.top"),sQuery(id+"F0.wireOp",EDGE,"E26.left"),sQuery(id+"F0.wireOp",EDGE,"E26.right"),sQuery(id+"F0.wireOp",EDGE,"E41"),sQuery(id+"F0.wireOp",EDGE,"E42"),sQuery(id+"F0.wireOp",EDGE,"E62"),sQuery(id+"F0.wireOp",EDGE,"E63.MirrorC"),sQuery(id+"F0.wireOp",EDGE,"E64.MirrorC"),sQuery(id+"F0.wireOp",EDGE,"E65.MirrorC"),sQuery(id+"F0.wireOp",EDGE,"E73"),sQuery(id+"F0.wireOp",EDGE,"E74"),sQuery(id+"F0.wireOp",EDGE,"E75.MirrorC"),sQuery(id+"F0.wireOp",EDGE,"E76.MirrorC"),sQuery(id+"F0.wireOp",EDGE,"E78.MirrorC"),sQuery(id+"F0.wireOp",EDGE,"E79.MirrorC"),sQuery(id+"F0.wireOp",EDGE,"E80.MirrorC"),sQuery(id+"F0.wireOp",EDGE,"E81.MirrorC"),sQuery(id+"F0.wireOp",EDGE,"E82.2.0.0"),sQuery(id+"F0.wireOp",EDGE,"E82.2.0.1"),sQuery(id+"F0.wireOp",EDGE,"E82.2.0.2"),sQuery(id+"F0.wireOp",EDGE,"E82.2.0.3"),sQuery(id+"F0.wireOp",EDGE,"E82.2.0.4"),sQuery(id+"F0.wireOp",EDGE,"E82.2.0.5"),sQuery(id+"F0.wireOp",EDGE,"E82.2.0.6"),sQuery(id+"F0.wireOp",EDGE,"E82.2.0.7"),sQuery(id+"F0.wireOp",EDGE,"E82.4.0.0"),sQuery(id+"F0.wireOp",EDGE,"E82.4.0.1"),sQuery(id+"F0.wireOp",EDGE,"E82.4.0.2"),sQuery(id+"F0.wireOp",EDGE,"E82.4.0.3"),sQuery(id+"F0.wireOp",EDGE,"E82.4.0.4"),sQuery(id+"F0.wireOp",EDGE,"E82.4.0.5"),sQuery(id+"F0.wireOp",EDGE,"E82.4.0.6"),sQuery(id+"F0.wireOp",EDGE,"E82.4.0.7"),sQuery(id+"F0.wireOp",EDGE,"E82.6.0.0"),sQuery(id+"F0.wireOp",EDGE,"E82.6.0.1"),sQuery(id+"F0.wireOp",EDGE,"E82.6.0.2"),sQuery(id+"F0.wireOp",EDGE,"E82.6.0.3"),sQuery(id+"F0.wireOp",EDGE,"E82.6.0.4"),sQuery(id+"F0.wireOp",EDGE,"E82.6.0.5"),sQuery(id+"F0.wireOp",EDGE,"E82.6.0.6"),sQuery(id+"F0.wireOp",EDGE,"E82.6.0.7"),sQuery(id+"F0.wireOp",EDGE,"E82.7.0.0"),sQuery(id+"F0.wireOp",EDGE,"E82.7.0.2"),sQuery(id+"F0.wireOp",EDGE,"E82.7.0.5"),sQuery(id+"F0.wireOp",EDGE,"E82.7.0.7")])]});
            transform(context, id + "F32", {"entities" : qUnion([Q0]), "transformType" : TransformType.TRANSLATION_3D, "dx" : 0 * mm, "dy" : 87.43 * mm, "dz" : 0 * mm, "makeCopy" : false});
        }
        {
            var Q0;
            Q0=makeQuery(id+"F2.opExtrude","SWEPT_BODY",BODY,{"disambiguationData":[OSD([sQuery(id+"F0.wireOp",EDGE,"E6"),sQuery(id+"F0.wireOp",EDGE,"E7.1.0.0"),sQuery(id+"F0.wireOp",EDGE,"E7.2.0.0"),sQuery(id+"F0.wireOp",EDGE,"E7.3.0.0"),sQuery(id+"F0.wireOp",EDGE,"E7.4.0.0"),sQuery(id+"F0.wireOp",EDGE,"E7.5.0.0"),sQuery(id+"F0.wireOp",EDGE,"E8"),sQuery(id+"F0.wireOp",EDGE,"E9.1.0.0"),sQuery(id+"F0.wireOp",EDGE,"E9.2.0.0"),sQuery(id+"F0.wireOp",EDGE,"E9.3.0.0"),sQuery(id+"F0.wireOp",EDGE,"E9.4.0.0"),sQuery(id+"F0.wireOp",EDGE,"E9.5.0.0"),sQuery(id+"F0.wireOp",EDGE,"E10.0.6.0"),sQuery(id+"F0.wireOp",EDGE,"E10.0.7.0"),sQuery(id+"F0.wireOp",EDGE,"E10.0.8.0"),sQuery(id+"F0.wireOp",EDGE,"E11.0.6.0"),sQuery(id+"F0.wireOp",EDGE,"E11.0.7.0"),sQuery(id+"F0.wireOp",EDGE,"E11.0.8.0"),sQuery(id+"F0.wireOp",EDGE,"E12.bottom"),sQuery(id+"F0.wireOp",EDGE,"E12.top"),sQuery(id+"F0.wireOp",EDGE,"E12.left"),sQuery(id+"F0.wireOp",EDGE,"E12.right"),sQuery(id+"F0.wireOp",EDGE,"E108"),sQuery(id+"F0.wireOp",EDGE,"E109"),sQuery(id+"F0.wireOp",EDGE,"E110"),sQuery(id+"F0.wireOp",EDGE,"E111")])]});
            transform(context, id + "F33", {"entities" : qUnion([Q0]), "transformType" : TransformType.TRANSLATION_3D, "dx" : 0 * mm, "dy" : 0 * mm, "dz" : -2.54 * mm, "makeCopy" : false});
        }
        {
            var Q0;
            Q0=makeQuery(id+"F2.opExtrude","SWEPT_BODY",BODY,{"disambiguationData":[OSD([sQuery(id+"F0.wireOp",EDGE,"E6"),sQuery(id+"F0.wireOp",EDGE,"E7.1.0.0"),sQuery(id+"F0.wireOp",EDGE,"E7.2.0.0"),sQuery(id+"F0.wireOp",EDGE,"E7.3.0.0"),sQuery(id+"F0.wireOp",EDGE,"E7.4.0.0"),sQuery(id+"F0.wireOp",EDGE,"E7.5.0.0"),sQuery(id+"F0.wireOp",EDGE,"E8"),sQuery(id+"F0.wireOp",EDGE,"E9.1.0.0"),sQuery(id+"F0.wireOp",EDGE,"E9.2.0.0"),sQuery(id+"F0.wireOp",EDGE,"E9.3.0.0"),sQuery(id+"F0.wireOp",EDGE,"E9.4.0.0"),sQuery(id+"F0.wireOp",EDGE,"E9.5.0.0"),sQuery(id+"F0.wireOp",EDGE,"E10.0.6.0"),sQuery(id+"F0.wireOp",EDGE,"E10.0.7.0"),sQuery(id+"F0.wireOp",EDGE,"E10.0.8.0"),sQuery(id+"F0.wireOp",EDGE,"E11.0.6.0"),sQuery(id+"F0.wireOp",EDGE,"E11.0.7.0"),sQuery(id+"F0.wireOp",EDGE,"E11.0.8.0"),sQuery(id+"F0.wireOp",EDGE,"E12.bottom"),sQuery(id+"F0.wireOp",EDGE,"E12.top"),sQuery(id+"F0.wireOp",EDGE,"E12.left"),sQuery(id+"F0.wireOp",EDGE,"E12.right"),sQuery(id+"F0.wireOp",EDGE,"E108"),sQuery(id+"F0.wireOp",EDGE,"E109"),sQuery(id+"F0.wireOp",EDGE,"E110"),sQuery(id+"F0.wireOp",EDGE,"E111")])]});
            transform(context, id + "F34", {"entities" : qUnion([Q0]), "transformType" : TransformType.TRANSLATION_3D, "dx" : 0 * mm, "dy" : 0 * mm, "dz" : -6.35 * mm, "makeCopy" : false});
        }
        {
            var Q0;
            Q0=makeQuery(id+"F4.opExtrude","SWEPT_BODY",BODY,{"disambiguationData":[OSD([sQuery(id+"F0.wireOp",EDGE,"E20"),sQuery(id+"F0.wireOp",EDGE,"E21.1.0.0"),sQuery(id+"F0.wireOp",EDGE,"E21.2.0.0"),sQuery(id+"F0.wireOp",EDGE,"E21.3.0.0"),sQuery(id+"F0.wireOp",EDGE,"E21.4.0.0"),sQuery(id+"F0.wireOp",EDGE,"E21.5.0.0"),sQuery(id+"F0.wireOp",EDGE,"E22"),sQuery(id+"F0.wireOp",EDGE,"E23.1.0.0"),sQuery(id+"F0.wireOp",EDGE,"E23.2.0.0"),sQuery(id+"F0.wireOp",EDGE,"E23.3.0.0"),sQuery(id+"F0.wireOp",EDGE,"E23.4.0.0"),sQuery(id+"F0.wireOp",EDGE,"E23.5.0.0"),sQuery(id+"F0.wireOp",EDGE,"E24.0.6.0"),sQuery(id+"F0.wireOp",EDGE,"E24.0.7.0"),sQuery(id+"F0.wireOp",EDGE,"E24.0.8.0"),sQuery(id+"F0.wireOp",EDGE,"E25.0.6.0"),sQuery(id+"F0.wireOp",EDGE,"E25.0.7.0"),sQuery(id+"F0.wireOp",EDGE,"E25.0.8.0"),sQuery(id+"F0.wireOp",EDGE,"E26.bottom"),sQuery(id+"F0.wireOp",EDGE,"E26.top"),sQuery(id+"F0.wireOp",EDGE,"E26.left"),sQuery(id+"F0.wireOp",EDGE,"E26.right"),sQuery(id+"F0.wireOp",EDGE,"E41"),sQuery(id+"F0.wireOp",EDGE,"E42"),sQuery(id+"F0.wireOp",EDGE,"E62"),sQuery(id+"F0.wireOp",EDGE,"E63.MirrorC"),sQuery(id+"F0.wireOp",EDGE,"E64.MirrorC"),sQuery(id+"F0.wireOp",EDGE,"E65.MirrorC"),sQuery(id+"F0.wireOp",EDGE,"E73"),sQuery(id+"F0.wireOp",EDGE,"E74"),sQuery(id+"F0.wireOp",EDGE,"E75.MirrorC"),sQuery(id+"F0.wireOp",EDGE,"E76.MirrorC"),sQuery(id+"F0.wireOp",EDGE,"E78.MirrorC"),sQuery(id+"F0.wireOp",EDGE,"E79.MirrorC"),sQuery(id+"F0.wireOp",EDGE,"E80.MirrorC"),sQuery(id+"F0.wireOp",EDGE,"E81.MirrorC"),sQuery(id+"F0.wireOp",EDGE,"E82.2.0.0"),sQuery(id+"F0.wireOp",EDGE,"E82.2.0.1"),sQuery(id+"F0.wireOp",EDGE,"E82.2.0.2"),sQuery(id+"F0.wireOp",EDGE,"E82.2.0.3"),sQuery(id+"F0.wireOp",EDGE,"E82.2.0.4"),sQuery(id+"F0.wireOp",EDGE,"E82.2.0.5"),sQuery(id+"F0.wireOp",EDGE,"E82.2.0.6"),sQuery(id+"F0.wireOp",EDGE,"E82.2.0.7"),sQuery(id+"F0.wireOp",EDGE,"E82.4.0.0"),sQuery(id+"F0.wireOp",EDGE,"E82.4.0.1"),sQuery(id+"F0.wireOp",EDGE,"E82.4.0.2"),sQuery(id+"F0.wireOp",EDGE,"E82.4.0.3"),sQuery(id+"F0.wireOp",EDGE,"E82.4.0.4"),sQuery(id+"F0.wireOp",EDGE,"E82.4.0.5"),sQuery(id+"F0.wireOp",EDGE,"E82.4.0.6"),sQuery(id+"F0.wireOp",EDGE,"E82.4.0.7"),sQuery(id+"F0.wireOp",EDGE,"E82.6.0.0"),sQuery(id+"F0.wireOp",EDGE,"E82.6.0.1"),sQuery(id+"F0.wireOp",EDGE,"E82.6.0.2"),sQuery(id+"F0.wireOp",EDGE,"E82.6.0.3"),sQuery(id+"F0.wireOp",EDGE,"E82.6.0.4"),sQuery(id+"F0.wireOp",EDGE,"E82.6.0.5"),sQuery(id+"F0.wireOp",EDGE,"E82.6.0.6"),sQuery(id+"F0.wireOp",EDGE,"E82.6.0.7"),sQuery(id+"F0.wireOp",EDGE,"E82.7.0.0"),sQuery(id+"F0.wireOp",EDGE,"E82.7.0.2"),sQuery(id+"F0.wireOp",EDGE,"E82.7.0.5"),sQuery(id+"F0.wireOp",EDGE,"E82.7.0.7")])]});
            var Q1;
            Q1=makeQuery(id+"F2.opExtrude","SWEPT_BODY",BODY,{"disambiguationData":[OSD([sQuery(id+"F0.wireOp",EDGE,"E6"),sQuery(id+"F0.wireOp",EDGE,"E7.1.0.0"),sQuery(id+"F0.wireOp",EDGE,"E7.2.0.0"),sQuery(id+"F0.wireOp",EDGE,"E7.3.0.0"),sQuery(id+"F0.wireOp",EDGE,"E7.4.0.0"),sQuery(id+"F0.wireOp",EDGE,"E7.5.0.0"),sQuery(id+"F0.wireOp",EDGE,"E8"),sQuery(id+"F0.wireOp",EDGE,"E9.1.0.0"),sQuery(id+"F0.wireOp",EDGE,"E9.2.0.0"),sQuery(id+"F0.wireOp",EDGE,"E9.3.0.0"),sQuery(id+"F0.wireOp",EDGE,"E9.4.0.0"),sQuery(id+"F0.wireOp",EDGE,"E9.5.0.0"),sQuery(id+"F0.wireOp",EDGE,"E10.0.6.0"),sQuery(id+"F0.wireOp",EDGE,"E10.0.7.0"),sQuery(id+"F0.wireOp",EDGE,"E10.0.8.0"),sQuery(id+"F0.wireOp",EDGE,"E11.0.6.0"),sQuery(id+"F0.wireOp",EDGE,"E11.0.7.0"),sQuery(id+"F0.wireOp",EDGE,"E11.0.8.0"),sQuery(id+"F0.wireOp",EDGE,"E12.bottom"),sQuery(id+"F0.wireOp",EDGE,"E12.top"),sQuery(id+"F0.wireOp",EDGE,"E12.left"),sQuery(id+"F0.wireOp",EDGE,"E12.right"),sQuery(id+"F0.wireOp",EDGE,"E108"),sQuery(id+"F0.wireOp",EDGE,"E109"),sQuery(id+"F0.wireOp",EDGE,"E110"),sQuery(id+"F0.wireOp",EDGE,"E111")])]});
            transform(context, id + "F35", {"entities" : qUnion([Q0, Q1]), "transformType" : TransformType.TRANSLATION_3D, "dx" : 0 * mm, "dy" : 0 * mm, "dz" : 1.27 * mm, "makeCopy" : false});
        }
        {
            var Q0;
            Q0=makeQuery(id+"F2.opExtrude","SWEPT_BODY",BODY,{"disambiguationData":[OSD([sQuery(id+"F0.wireOp",EDGE,"E6"),sQuery(id+"F0.wireOp",EDGE,"E7.1.0.0"),sQuery(id+"F0.wireOp",EDGE,"E7.2.0.0"),sQuery(id+"F0.wireOp",EDGE,"E7.3.0.0"),sQuery(id+"F0.wireOp",EDGE,"E7.4.0.0"),sQuery(id+"F0.wireOp",EDGE,"E7.5.0.0"),sQuery(id+"F0.wireOp",EDGE,"E8"),sQuery(id+"F0.wireOp",EDGE,"E9.1.0.0"),sQuery(id+"F0.wireOp",EDGE,"E9.2.0.0"),sQuery(id+"F0.wireOp",EDGE,"E9.3.0.0"),sQuery(id+"F0.wireOp",EDGE,"E9.4.0.0"),sQuery(id+"F0.wireOp",EDGE,"E9.5.0.0"),sQuery(id+"F0.wireOp",EDGE,"E10.0.6.0"),sQuery(id+"F0.wireOp",EDGE,"E10.0.7.0"),sQuery(id+"F0.wireOp",EDGE,"E10.0.8.0"),sQuery(id+"F0.wireOp",EDGE,"E11.0.6.0"),sQuery(id+"F0.wireOp",EDGE,"E11.0.7.0"),sQuery(id+"F0.wireOp",EDGE,"E11.0.8.0"),sQuery(id+"F0.wireOp",EDGE,"E12.bottom"),sQuery(id+"F0.wireOp",EDGE,"E12.top"),sQuery(id+"F0.wireOp",EDGE,"E12.left"),sQuery(id+"F0.wireOp",EDGE,"E12.right"),sQuery(id+"F0.wireOp",EDGE,"E108"),sQuery(id+"F0.wireOp",EDGE,"E109"),sQuery(id+"F0.wireOp",EDGE,"E110"),sQuery(id+"F0.wireOp",EDGE,"E111")])]});
            transform(context, id + "F36", {"entities" : qUnion([Q0]), "transformType" : TransformType.TRANSLATION_3D, "dx" : 0 * mm, "dy" : 0 * mm, "dz" : -1.27 * mm, "makeCopy" : false});
        }
        {
            var Q0;
            Q0=makeQuery(id+"F3.opExtrude","SWEPT_BODY",BODY,{"disambiguationData":[OSD([sQuery(id+"F0.wireOp",EDGE,"E13"),sQuery(id+"F0.wireOp",EDGE,"E14.1.0.0"),sQuery(id+"F0.wireOp",EDGE,"E14.2.0.0"),sQuery(id+"F0.wireOp",EDGE,"E14.3.0.0"),sQuery(id+"F0.wireOp",EDGE,"E14.4.0.0"),sQuery(id+"F0.wireOp",EDGE,"E14.5.0.0"),sQuery(id+"F0.wireOp",EDGE,"E15"),sQuery(id+"F0.wireOp",EDGE,"E16.1.0.0"),sQuery(id+"F0.wireOp",EDGE,"E16.2.0.0"),sQuery(id+"F0.wireOp",EDGE,"E16.3.0.0"),sQuery(id+"F0.wireOp",EDGE,"E16.4.0.0"),sQuery(id+"F0.wireOp",EDGE,"E16.5.0.0"),sQuery(id+"F0.wireOp",EDGE,"E17.0.6.0"),sQuery(id+"F0.wireOp",EDGE,"E17.0.7.0"),sQuery(id+"F0.wireOp",EDGE,"E17.0.8.0"),sQuery(id+"F0.wireOp",EDGE,"E18.0.6.0"),sQuery(id+"F0.wireOp",EDGE,"E18.0.7.0"),sQuery(id+"F0.wireOp",EDGE,"E18.0.8.0"),sQuery(id+"F0.wireOp",EDGE,"E19.bottom"),sQuery(id+"F0.wireOp",EDGE,"E19.top"),sQuery(id+"F0.wireOp",EDGE,"E19.left"),sQuery(id+"F0.wireOp",EDGE,"E19.right"),sQuery(id+"F0.wireOp",EDGE,"E36"),sQuery(id+"F0.wireOp",EDGE,"E38"),sQuery(id+"F0.wireOp",EDGE,"E69.MirrorC"),sQuery(id+"F0.wireOp",EDGE,"E70.MirrorC"),sQuery(id+"F0.wireOp",EDGE,"E71.MirrorC"),sQuery(id+"F0.wireOp",EDGE,"E72.MirrorC"),sQuery(id+"F0.wireOp",EDGE,"E83.MirrorC"),sQuery(id+"F0.wireOp",EDGE,"E84.MirrorC"),sQuery(id+"F0.wireOp",EDGE,"E85.MirrorC"),sQuery(id+"F0.wireOp",EDGE,"E86.MirrorC"),sQuery(id+"F0.wireOp",EDGE,"E87.MirrorC"),sQuery(id+"F0.wireOp",EDGE,"E88.MirrorC"),sQuery(id+"F0.wireOp",EDGE,"E89.MirrorC"),sQuery(id+"F0.wireOp",EDGE,"E90.MirrorC"),sQuery(id+"F0.wireOp",EDGE,"E91.MirrorC"),sQuery(id+"F0.wireOp",EDGE,"E92.MirrorC"),sQuery(id+"F0.wireOp",EDGE,"E93.MirrorC"),sQuery(id+"F0.wireOp",EDGE,"E94.MirrorC"),sQuery(id+"F0.wireOp",EDGE,"E96.MirrorC"),sQuery(id+"F0.wireOp",EDGE,"E97.MirrorC"),sQuery(id+"F0.wireOp",EDGE,"E98.MirrorC"),sQuery(id+"F0.wireOp",EDGE,"E99.MirrorC"),sQuery(id+"F0.wireOp",EDGE,"E95.MirrorC"),sQuery(id+"F0.wireOp",EDGE,"E100.MirrorC")])]});
            transform(context, id + "F37", {"entities" : qUnion([Q0]), "transformType" : TransformType.TRANSLATION_3D, "dx" : 0 * mm, "dy" : 0 * mm, "dz" : -2.16 * mm, "makeCopy" : false});
        }
        {
            var Q0;
            {var subQ2=sQuery(id+"F0.wireOp",EDGE,"E82.7.0.0");var subQ3=sQuery(id+"F0.wireOp",EDGE,"E82.4.0.0");var subQ4=sQuery(id+"F0.wireOp",EDGE,"E64.MirrorC");var subQ7=sQuery(id+"F0.wireOp",EDGE,"E82.7.0.5");var subQ8=sQuery(id+"F0.wireOp",EDGE,"E82.6.0.6");var subQ9=sQuery(id+"F0.wireOp",EDGE,"E82.6.0.5");var subQ10=sQuery(id+"F0.wireOp",EDGE,"E82.6.0.1");var subQ11=sQuery(id+"F0.wireOp",EDGE,"E82.6.0.0");var subQ12=sQuery(id+"F0.wireOp",EDGE,"E82.4.0.6");var subQ13=sQuery(id+"F0.wireOp",EDGE,"E82.4.0.5");var subQ14=sQuery(id+"F0.wireOp",EDGE,"E82.4.0.1");var subQ15=sQuery(id+"F0.wireOp",EDGE,"E82.2.0.6");var subQ16=sQuery(id+"F0.wireOp",EDGE,"E82.2.0.5");var subQ17=sQuery(id+"F0.wireOp",EDGE,"E82.2.0.1");var subQ18=sQuery(id+"F0.wireOp",EDGE,"E82.2.0.0");var subQ19=sQuery(id+"F0.wireOp",EDGE,"E81.MirrorC");var subQ20=sQuery(id+"F0.wireOp",EDGE,"E78.MirrorC");var subQ21=sQuery(id+"F0.wireOp",EDGE,"E76.MirrorC");var subQ22=sQuery(id+"F0.wireOp",EDGE,"E74");var subQ23=sQuery(id+"F0.wireOp",EDGE,"E65.MirrorC");var subQ24=sQuery(id+"F0.wireOp",EDGE,"E63.MirrorC");var subQ25=sQuery(id+"F0.wireOp",EDGE,"E62");var subQ26=sQuery(id+"F0.wireOp",EDGE,"E42");var subQ27=sQuery(id+"F0.wireOp",EDGE,"E41");var subQ28=sQuery(id+"F0.wireOp",EDGE,"E26.right");var subQ29=sQuery(id+"F0.wireOp",EDGE,"E26.left");var subQ30=sQuery(id+"F0.wireOp",EDGE,"E26.top");var subQ31=sQuery(id+"F0.wireOp",EDGE,"E26.bottom");var subQ32=sQuery(id+"F0.wireOp",EDGE,"E25.0.8.0");var subQ33=sQuery(id+"F0.wireOp",EDGE,"E25.0.7.0");var subQ34=sQuery(id+"F0.wireOp",EDGE,"E25.0.6.0");var subQ35=sQuery(id+"F0.wireOp",EDGE,"E24.0.8.0");var subQ36=sQuery(id+"F0.wireOp",EDGE,"E24.0.7.0");var subQ37=sQuery(id+"F0.wireOp",EDGE,"E24.0.6.0");var subQ38=sQuery(id+"F0.wireOp",EDGE,"E23.5.0.0");var subQ39=sQuery(id+"F0.wireOp",EDGE,"E23.4.0.0");var subQ40=sQuery(id+"F0.wireOp",EDGE,"E23.3.0.0");var subQ41=sQuery(id+"F0.wireOp",EDGE,"E23.2.0.0");var subQ42=sQuery(id+"F0.wireOp",EDGE,"E23.1.0.0");var subQ43=sQuery(id+"F0.wireOp",EDGE,"E22");var subQ44=sQuery(id+"F0.wireOp",EDGE,"E21.5.0.0");var subQ45=sQuery(id+"F0.wireOp",EDGE,"E21.4.0.0");var subQ46=sQuery(id+"F0.wireOp",EDGE,"E21.3.0.0");var subQ47=sQuery(id+"F0.wireOp",EDGE,"E21.2.0.0");var subQ48=sQuery(id+"F0.wireOp",EDGE,"E21.1.0.0");var subQ49=sQuery(id+"F0.wireOp",EDGE,"E20");var subQ50=makeQuery(id+"F4.opExtrude","CAP_FACE",FACE,{"disambiguationData":[OSD([subQ49,subQ48,subQ47,subQ46,subQ45,subQ44,subQ43,subQ42,subQ41,subQ40,subQ39,subQ38,subQ37,subQ36,subQ35,subQ34,subQ33,subQ32,subQ31,subQ30,subQ29,subQ28,subQ27,subQ26,subQ25,subQ24,subQ4,subQ23,sQuery(id+"F0.wireOp",EDGE,"E73"),subQ22,sQuery(id+"F0.wireOp",EDGE,"E75.MirrorC"),subQ21,subQ20,sQuery(id+"F0.wireOp",EDGE,"E79.MirrorC"),sQuery(id+"F0.wireOp",EDGE,"E80.MirrorC"),subQ19,subQ18,subQ17,sQuery(id+"F0.wireOp",EDGE,"E82.2.0.2"),sQuery(id+"F0.wireOp",EDGE,"E82.2.0.3"),sQuery(id+"F0.wireOp",EDGE,"E82.2.0.4"),subQ16,subQ15,sQuery(id+"F0.wireOp",EDGE,"E82.2.0.7"),subQ3,subQ14,sQuery(id+"F0.wireOp",EDGE,"E82.4.0.2"),sQuery(id+"F0.wireOp",EDGE,"E82.4.0.3"),sQuery(id+"F0.wireOp",EDGE,"E82.4.0.4"),subQ13,subQ12,sQuery(id+"F0.wireOp",EDGE,"E82.4.0.7"),subQ11,subQ10,sQuery(id+"F0.wireOp",EDGE,"E82.6.0.2"),sQuery(id+"F0.wireOp",EDGE,"E82.6.0.3"),sQuery(id+"F0.wireOp",EDGE,"E82.6.0.4"),subQ9,subQ8,sQuery(id+"F0.wireOp",EDGE,"E82.6.0.7"),subQ2,sQuery(id+"F0.wireOp",EDGE,"E82.7.0.2"),subQ7,sQuery(id+"F0.wireOp",EDGE,"E82.7.0.7")])],"isStart":true});Q0=makeQuery(id+"F14.boolean.opBoolean","SPLIT",FACE,{"disambiguationData":[TD([makeQuery(id+"F4.opExtrude","SWEPT_FACE",FACE,{"disambiguationData":[OSD([subQ31])]})])],"derivedFrom":subQ50});}
            var sketch = newSketch(context, id + "F38", { "sketchPlane" : qUnion([Q0])});
            skPoint(sketch, "E177.first.point", {"position": v(164.24, -29.7) * mm});
            skPoint(sketch, "E177.second.point", {"position": v(175.72, -19.95) * mm});
            skPoint(sketch, "E177.third.point", {"position": v(159.07, -26.02) * mm});
            skPoint(sketch, "E178.first.point", {"position": v(153.71, -25.44) * mm});
            skPoint(sketch, "E178.second.point", {"position": v(143.4, -29.7) * mm});
            skPoint(sketch, "E178.third.point", {"position": v(137.88, -25.44) * mm});
            skCircle(sketch, "E179", {"center": v(166.62, -20.87) * mm, "radius": 9.27 * mm});
            skLineSegment(sketch, "E180", {"start": v(178.3, -10.46) * mm, "end": v(114.33, -10.46) * mm, "construction": true});
            skCircle(sketch, "E181.MirrorC", {"center": v(166.62, -0.04) * mm, "radius": 9.27 * mm});
            skCircle(sketch, "E182.1.0.0", {"center": v(145.8, -20.87) * mm, "radius": 9.27 * mm});
            skCircle(sketch, "E182.1.0.1", {"center": v(145.8, -0.04) * mm, "radius": 9.27 * mm});
            skCircle(sketch, "E182.2.0.0", {"center": v(124.97, -20.87) * mm, "radius": 9.27 * mm});
            skCircle(sketch, "E182.2.0.1", {"center": v(124.97, -0.04) * mm, "radius": 9.27 * mm});
            skCircle(sketch, "E182.3.0.0", {"center": v(104.14, -20.87) * mm, "radius": 9.27 * mm});
            skCircle(sketch, "E182.3.0.1", {"center": v(104.14, -0.04) * mm, "radius": 9.27 * mm});
            skCircle(sketch, "E182.4.0.0", {"center": v(83.31, -20.87) * mm, "radius": 9.27 * mm});
            skCircle(sketch, "E182.4.0.1", {"center": v(83.31, -0.04) * mm, "radius": 9.27 * mm});
            skCircle(sketch, "E182.5.0.0", {"center": v(62.48, -20.87) * mm, "radius": 9.27 * mm});
            skCircle(sketch, "E182.5.0.1", {"center": v(62.48, -0.04) * mm, "radius": 9.27 * mm});
            skCircle(sketch, "E182.6.0.0", {"center": v(41.66, -20.87) * mm, "radius": 9.27 * mm});
            skCircle(sketch, "E182.6.0.1", {"center": v(41.66, -0.04) * mm, "radius": 9.27 * mm});
            skCircle(sketch, "E182.7.0.0", {"center": v(20.83, -20.87) * mm, "radius": 9.27 * mm});
            skCircle(sketch, "E182.7.0.1", {"center": v(20.83, -0.04) * mm, "radius": 9.27 * mm});
            skCircle(sketch, "E182.8.0.0", {"center": v(0, -20.87) * mm, "radius": 9.27 * mm});
            skCircle(sketch, "E182.8.0.1", {"center": v(0, -0.04) * mm, "radius": 9.27 * mm});
            skLineSegment(sketch, "E182.direction1", {"start": v(166.62, -20.87) * mm, "end": v(145.8, -20.87) * mm, "construction": true});
            skSolve(sketch);
        }
        {
            var Q0;
            Q0 = qSketchRegion(id + "F38", true);
            extrude(context, id + "F39", {"entities" : qUnion([Q0]), "operationType" : NewBodyOperationType.REMOVE, "oppositeDirection" : true, "depth" : 10.16 * mm, "offsetDistance" : 25.4 * mm});
        }
        {
            var Q0;
            {var subQ6=sQuery(id+"F0.wireOp",EDGE,"E11.0.6.0");var subQ8=sQuery(id+"F0.wireOp",EDGE,"E7.5.0.0");var subQ10=sQuery(id+"F0.wireOp",EDGE,"E111");var subQ11=sQuery(id+"F0.wireOp",EDGE,"E110");var subQ12=sQuery(id+"F0.wireOp",EDGE,"E109");var subQ13=sQuery(id+"F0.wireOp",EDGE,"E108");var subQ14=sQuery(id+"F0.wireOp",EDGE,"E12.right");var subQ15=sQuery(id+"F0.wireOp",EDGE,"E12.left");var subQ16=sQuery(id+"F0.wireOp",EDGE,"E12.top");var subQ17=sQuery(id+"F0.wireOp",EDGE,"E12.bottom");var subQ18=sQuery(id+"F0.wireOp",EDGE,"E11.0.8.0");var subQ19=sQuery(id+"F0.wireOp",EDGE,"E11.0.7.0");var subQ20=sQuery(id+"F0.wireOp",EDGE,"E10.0.8.0");var subQ21=sQuery(id+"F0.wireOp",EDGE,"E10.0.7.0");var subQ22=sQuery(id+"F0.wireOp",EDGE,"E10.0.6.0");var subQ23=sQuery(id+"F0.wireOp",EDGE,"E9.5.0.0");var subQ24=sQuery(id+"F0.wireOp",EDGE,"E9.4.0.0");var subQ25=sQuery(id+"F0.wireOp",EDGE,"E9.3.0.0");var subQ26=sQuery(id+"F0.wireOp",EDGE,"E9.2.0.0");var subQ27=sQuery(id+"F0.wireOp",EDGE,"E9.1.0.0");var subQ28=sQuery(id+"F0.wireOp",EDGE,"E8");var subQ29=sQuery(id+"F0.wireOp",EDGE,"E7.4.0.0");var subQ30=sQuery(id+"F0.wireOp",EDGE,"E7.3.0.0");var subQ31=sQuery(id+"F0.wireOp",EDGE,"E7.2.0.0");var subQ32=sQuery(id+"F0.wireOp",EDGE,"E7.1.0.0");var subQ33=makeQuery(id+"F2.opExtrude","CAP_FACE",FACE,{"disambiguationData":[OSD([sQuery(id+"F0.wireOp",EDGE,"E6"),subQ32,subQ31,subQ30,subQ29,subQ8,subQ28,subQ27,subQ26,subQ25,subQ24,subQ23,subQ22,subQ21,subQ20,subQ6,subQ19,subQ18,subQ17,subQ16,subQ15,subQ14,subQ13,subQ12,subQ11,subQ10])],"isStart":false});Q0=makeQuery(id+"F21.boolean.opBoolean","SPLIT",FACE,{"disambiguationData":[TD([makeQuery(id+"F2.opExtrude","SWEPT_FACE",FACE,{"disambiguationData":[OSD([subQ17])]})])],"derivedFrom":subQ33});}
            var sketch = newSketch(context, id + "F40", { "sketchPlane" : qUnion([Q0])});
            skPoint(sketch, "E183.first.point", {"position": v(162, -7.85) * mm});
            skPoint(sketch, "E183.second.point", {"position": v(175.63, -1.56) * mm});
            skPoint(sketch, "E183.third.point", {"position": v(173.48, 6.08) * mm});
            skCircle(sketch, "E184", {"center": v(166.62, 0.04) * mm, "radius": 9.27 * mm});
            skLineSegment(sketch, "E185", {"start": v(178.3, 10.45) * mm, "end": v(138.33, 10.45) * mm, "construction": true});
            skCircle(sketch, "E186.MirrorC", {"center": v(166.62, 20.86) * mm, "radius": 9.27 * mm});
            skCircle(sketch, "E187.1.0.0", {"center": v(145.8, 0.04) * mm, "radius": 9.27 * mm});
            skCircle(sketch, "E187.1.0.1", {"center": v(145.8, 20.86) * mm, "radius": 9.27 * mm});
            skCircle(sketch, "E187.2.0.0", {"center": v(124.97, 0.04) * mm, "radius": 9.27 * mm});
            skCircle(sketch, "E187.2.0.1", {"center": v(124.97, 20.86) * mm, "radius": 9.27 * mm});
            skCircle(sketch, "E187.3.0.0", {"center": v(104.14, 0.04) * mm, "radius": 9.27 * mm});
            skCircle(sketch, "E187.3.0.1", {"center": v(104.14, 20.86) * mm, "radius": 9.27 * mm});
            skCircle(sketch, "E187.4.0.0", {"center": v(83.31, 0.04) * mm, "radius": 9.27 * mm});
            skCircle(sketch, "E187.4.0.1", {"center": v(83.31, 20.86) * mm, "radius": 9.27 * mm});
            skCircle(sketch, "E187.5.0.0", {"center": v(62.48, 0.04) * mm, "radius": 9.27 * mm});
            skCircle(sketch, "E187.5.0.1", {"center": v(62.48, 20.86) * mm, "radius": 9.27 * mm});
            skCircle(sketch, "E187.6.0.0", {"center": v(41.66, 0.04) * mm, "radius": 9.27 * mm});
            skCircle(sketch, "E187.6.0.1", {"center": v(41.66, 20.86) * mm, "radius": 9.27 * mm});
            skCircle(sketch, "E187.7.0.0", {"center": v(20.83, 0.04) * mm, "radius": 9.27 * mm});
            skCircle(sketch, "E187.7.0.1", {"center": v(20.83, 20.86) * mm, "radius": 9.27 * mm});
            skCircle(sketch, "E187.8.0.0", {"center": v(0, 0.04) * mm, "radius": 9.27 * mm});
            skCircle(sketch, "E187.8.0.1", {"center": v(0, 20.86) * mm, "radius": 9.27 * mm});
            skLineSegment(sketch, "E187.direction1", {"start": v(166.62, 0.04) * mm, "end": v(145.8, 0.04) * mm, "construction": true});
            skSolve(sketch);
        }
        {
            var Q0;
            Q0 = qSketchRegion(id + "F40", true);
            extrude(context, id + "F41", {"entities" : qUnion([Q0]), "operationType" : NewBodyOperationType.REMOVE, "oppositeDirection" : true, "depth" : 10.16 * mm, "offsetDistance" : 25.4 * mm});
        }
        {
            var Q0;
            Q0=makeQuery(id+"F3.opExtrude","CAP_FACE",FACE,{"disambiguationData":[OSD([sQuery(id+"F0.wireOp",EDGE,"E13"),sQuery(id+"F0.wireOp",EDGE,"E14.1.0.0"),sQuery(id+"F0.wireOp",EDGE,"E14.2.0.0"),sQuery(id+"F0.wireOp",EDGE,"E14.3.0.0"),sQuery(id+"F0.wireOp",EDGE,"E14.4.0.0"),sQuery(id+"F0.wireOp",EDGE,"E14.5.0.0"),sQuery(id+"F0.wireOp",EDGE,"E15"),sQuery(id+"F0.wireOp",EDGE,"E16.1.0.0"),sQuery(id+"F0.wireOp",EDGE,"E16.2.0.0"),sQuery(id+"F0.wireOp",EDGE,"E16.3.0.0"),sQuery(id+"F0.wireOp",EDGE,"E16.4.0.0"),sQuery(id+"F0.wireOp",EDGE,"E16.5.0.0"),sQuery(id+"F0.wireOp",EDGE,"E17.0.6.0"),sQuery(id+"F0.wireOp",EDGE,"E17.0.7.0"),sQuery(id+"F0.wireOp",EDGE,"E17.0.8.0"),sQuery(id+"F0.wireOp",EDGE,"E18.0.6.0"),sQuery(id+"F0.wireOp",EDGE,"E18.0.7.0"),sQuery(id+"F0.wireOp",EDGE,"E18.0.8.0"),sQuery(id+"F0.wireOp",EDGE,"E19.bottom"),sQuery(id+"F0.wireOp",EDGE,"E19.top"),sQuery(id+"F0.wireOp",EDGE,"E19.left"),sQuery(id+"F0.wireOp",EDGE,"E19.right"),sQuery(id+"F0.wireOp",EDGE,"E36"),sQuery(id+"F0.wireOp",EDGE,"E38"),sQuery(id+"F0.wireOp",EDGE,"E69.MirrorC"),sQuery(id+"F0.wireOp",EDGE,"E70.MirrorC"),sQuery(id+"F0.wireOp",EDGE,"E71.MirrorC"),sQuery(id+"F0.wireOp",EDGE,"E72.MirrorC"),sQuery(id+"F0.wireOp",EDGE,"E83.MirrorC"),sQuery(id+"F0.wireOp",EDGE,"E84.MirrorC"),sQuery(id+"F0.wireOp",EDGE,"E85.MirrorC"),sQuery(id+"F0.wireOp",EDGE,"E86.MirrorC"),sQuery(id+"F0.wireOp",EDGE,"E87.MirrorC"),sQuery(id+"F0.wireOp",EDGE,"E88.MirrorC"),sQuery(id+"F0.wireOp",EDGE,"E89.MirrorC"),sQuery(id+"F0.wireOp",EDGE,"E90.MirrorC"),sQuery(id+"F0.wireOp",EDGE,"E91.MirrorC"),sQuery(id+"F0.wireOp",EDGE,"E92.MirrorC"),sQuery(id+"F0.wireOp",EDGE,"E93.MirrorC"),sQuery(id+"F0.wireOp",EDGE,"E94.MirrorC"),sQuery(id+"F0.wireOp",EDGE,"E96.MirrorC"),sQuery(id+"F0.wireOp",EDGE,"E97.MirrorC"),sQuery(id+"F0.wireOp",EDGE,"E98.MirrorC"),sQuery(id+"F0.wireOp",EDGE,"E99.MirrorC"),sQuery(id+"F0.wireOp",EDGE,"E95.MirrorC"),sQuery(id+"F0.wireOp",EDGE,"E100.MirrorC")])],"isStart":false});
            var sketch = newSketch(context, id + "F42", { "sketchPlane" : qUnion([Q0])});
            skPoint(sketch, "E188.first.point", {"position": v(160.35, -6.62) * mm});
            skPoint(sketch, "E188.second.point", {"position": v(175.72, -0.86) * mm});
            skPoint(sketch, "E188.third.point", {"position": v(163.6, 8.66) * mm});
            skCircle(sketch, "E189", {"center": v(166.62, 0.03) * mm, "radius": 9.27 * mm});
            skLineSegment(sketch, "E190", {"start": v(178.3, 10.44) * mm, "end": v(145.72, 10.44) * mm, "construction": true});
            skCircle(sketch, "E191.MirrorC", {"center": v(166.62, 20.85) * mm, "radius": 9.27 * mm});
            skCircle(sketch, "E192.1.0.0", {"center": v(145.8, 0.03) * mm, "radius": 9.27 * mm});
            skCircle(sketch, "E192.1.0.1", {"center": v(145.8, 20.85) * mm, "radius": 9.27 * mm});
            skCircle(sketch, "E192.2.0.0", {"center": v(124.97, 0.03) * mm, "radius": 9.27 * mm});
            skCircle(sketch, "E192.2.0.1", {"center": v(124.97, 20.85) * mm, "radius": 9.27 * mm});
            skCircle(sketch, "E192.3.0.0", {"center": v(104.14, 0.03) * mm, "radius": 9.27 * mm});
            skCircle(sketch, "E192.3.0.1", {"center": v(104.14, 20.85) * mm, "radius": 9.27 * mm});
            skCircle(sketch, "E192.4.0.0", {"center": v(83.31, 0.03) * mm, "radius": 9.27 * mm});
            skCircle(sketch, "E192.4.0.1", {"center": v(83.31, 20.85) * mm, "radius": 9.27 * mm});
            skCircle(sketch, "E192.5.0.0", {"center": v(62.48, 0.03) * mm, "radius": 9.27 * mm});
            skCircle(sketch, "E192.5.0.1", {"center": v(62.48, 20.85) * mm, "radius": 9.27 * mm});
            skCircle(sketch, "E192.6.0.0", {"center": v(41.66, 0.03) * mm, "radius": 9.27 * mm});
            skCircle(sketch, "E192.6.0.1", {"center": v(41.66, 20.85) * mm, "radius": 9.27 * mm});
            skCircle(sketch, "E192.7.0.0", {"center": v(20.83, 0.03) * mm, "radius": 9.27 * mm});
            skCircle(sketch, "E192.7.0.1", {"center": v(20.83, 20.85) * mm, "radius": 9.27 * mm});
            skCircle(sketch, "E192.8.0.0", {"center": v(0, 0.03) * mm, "radius": 9.27 * mm});
            skCircle(sketch, "E192.8.0.1", {"center": v(0, 20.85) * mm, "radius": 9.27 * mm});
            skLineSegment(sketch, "E192.direction1", {"start": v(166.62, 0.03) * mm, "end": v(145.8, 0.03) * mm, "construction": true});
            skSolve(sketch);
        }
        {
            var Q0;
            Q0 = qSketchRegion(id + "F42", true);
            extrude(context, id + "F43", {"entities" : qUnion([Q0]), "operationType" : NewBodyOperationType.REMOVE, "oppositeDirection" : true, "depth" : 10.16 * mm, "offsetDistance" : 25.4 * mm});
        }
        {
            var Q0;
            Q0=makeQuery(id+"F3.opExtrude","CAP_FACE",FACE,{"disambiguationData":[OSD([sQuery(id+"F0.wireOp",EDGE,"E13"),sQuery(id+"F0.wireOp",EDGE,"E14.1.0.0"),sQuery(id+"F0.wireOp",EDGE,"E14.2.0.0"),sQuery(id+"F0.wireOp",EDGE,"E14.3.0.0"),sQuery(id+"F0.wireOp",EDGE,"E14.4.0.0"),sQuery(id+"F0.wireOp",EDGE,"E14.5.0.0"),sQuery(id+"F0.wireOp",EDGE,"E15"),sQuery(id+"F0.wireOp",EDGE,"E16.1.0.0"),sQuery(id+"F0.wireOp",EDGE,"E16.2.0.0"),sQuery(id+"F0.wireOp",EDGE,"E16.3.0.0"),sQuery(id+"F0.wireOp",EDGE,"E16.4.0.0"),sQuery(id+"F0.wireOp",EDGE,"E16.5.0.0"),sQuery(id+"F0.wireOp",EDGE,"E17.0.6.0"),sQuery(id+"F0.wireOp",EDGE,"E17.0.7.0"),sQuery(id+"F0.wireOp",EDGE,"E17.0.8.0"),sQuery(id+"F0.wireOp",EDGE,"E18.0.6.0"),sQuery(id+"F0.wireOp",EDGE,"E18.0.7.0"),sQuery(id+"F0.wireOp",EDGE,"E18.0.8.0"),sQuery(id+"F0.wireOp",EDGE,"E19.bottom"),sQuery(id+"F0.wireOp",EDGE,"E19.top"),sQuery(id+"F0.wireOp",EDGE,"E19.left"),sQuery(id+"F0.wireOp",EDGE,"E19.right"),sQuery(id+"F0.wireOp",EDGE,"E36"),sQuery(id+"F0.wireOp",EDGE,"E38"),sQuery(id+"F0.wireOp",EDGE,"E69.MirrorC"),sQuery(id+"F0.wireOp",EDGE,"E70.MirrorC"),sQuery(id+"F0.wireOp",EDGE,"E71.MirrorC"),sQuery(id+"F0.wireOp",EDGE,"E72.MirrorC"),sQuery(id+"F0.wireOp",EDGE,"E83.MirrorC"),sQuery(id+"F0.wireOp",EDGE,"E84.MirrorC"),sQuery(id+"F0.wireOp",EDGE,"E85.MirrorC"),sQuery(id+"F0.wireOp",EDGE,"E86.MirrorC"),sQuery(id+"F0.wireOp",EDGE,"E87.MirrorC"),sQuery(id+"F0.wireOp",EDGE,"E88.MirrorC"),sQuery(id+"F0.wireOp",EDGE,"E89.MirrorC"),sQuery(id+"F0.wireOp",EDGE,"E90.MirrorC"),sQuery(id+"F0.wireOp",EDGE,"E91.MirrorC"),sQuery(id+"F0.wireOp",EDGE,"E92.MirrorC"),sQuery(id+"F0.wireOp",EDGE,"E93.MirrorC"),sQuery(id+"F0.wireOp",EDGE,"E94.MirrorC"),sQuery(id+"F0.wireOp",EDGE,"E96.MirrorC"),sQuery(id+"F0.wireOp",EDGE,"E97.MirrorC"),sQuery(id+"F0.wireOp",EDGE,"E98.MirrorC"),sQuery(id+"F0.wireOp",EDGE,"E99.MirrorC"),sQuery(id+"F0.wireOp",EDGE,"E95.MirrorC"),sQuery(id+"F0.wireOp",EDGE,"E100.MirrorC")])],"isStart":false});
            var sketch = newSketch(context, id + "F44", { "sketchPlane" : qUnion([Q0])});
            skPoint(sketch, "E193.first.point", {"position": v(6.22, 27.73) * mm});
            skPoint(sketch, "E193.second.point", {"position": v(-9.11, 19.14) * mm});
            skPoint(sketch, "E193.third.point", {"position": v(5.43, 13.34) * mm});
            skPoint(sketch, "E194.first.point", {"position": v(5.72, 7.32) * mm});
            skPoint(sketch, "E194.second.point", {"position": v(-8.52, 3.67) * mm});
            skPoint(sketch, "E194.third.point", {"position": v(5.45, -7.47) * mm});
            skCircle(sketch, "E195", {"center": v(0, 20.85) * mm, "radius": 9.33 * mm});
            skCircle(sketch, "E196", {"center": v(0, 0.03) * mm, "radius": 9.33 * mm});
            skCircle(sketch, "E197.1.0.0", {"center": v(20.83, 20.85) * mm, "radius": 9.33 * mm});
            skCircle(sketch, "E197.1.0.1", {"center": v(20.83, 0.03) * mm, "radius": 9.33 * mm});
            skCircle(sketch, "E197.2.0.0", {"center": v(41.66, 20.85) * mm, "radius": 9.33 * mm});
            skCircle(sketch, "E197.2.0.1", {"center": v(41.66, 0.03) * mm, "radius": 9.33 * mm});
            skCircle(sketch, "E197.3.0.0", {"center": v(62.48, 20.85) * mm, "radius": 9.33 * mm});
            skCircle(sketch, "E197.3.0.1", {"center": v(62.48, 0.03) * mm, "radius": 9.33 * mm});
            skCircle(sketch, "E197.4.0.0", {"center": v(83.31, 20.85) * mm, "radius": 9.33 * mm});
            skCircle(sketch, "E197.4.0.1", {"center": v(83.31, 0.03) * mm, "radius": 9.33 * mm});
            skCircle(sketch, "E197.5.0.0", {"center": v(104.14, 20.85) * mm, "radius": 9.33 * mm});
            skCircle(sketch, "E197.5.0.1", {"center": v(104.14, 0.03) * mm, "radius": 9.33 * mm});
            skCircle(sketch, "E197.6.0.0", {"center": v(124.97, 20.85) * mm, "radius": 9.33 * mm});
            skCircle(sketch, "E197.6.0.1", {"center": v(124.97, 0.03) * mm, "radius": 9.33 * mm});
            skCircle(sketch, "E197.7.0.0", {"center": v(145.8, 20.85) * mm, "radius": 9.33 * mm});
            skCircle(sketch, "E197.7.0.1", {"center": v(145.8, 0.03) * mm, "radius": 9.33 * mm});
            skCircle(sketch, "E197.8.0.0", {"center": v(166.62, 20.85) * mm, "radius": 9.33 * mm});
            skCircle(sketch, "E197.8.0.1", {"center": v(166.62, 0.03) * mm, "radius": 9.33 * mm});
            skLineSegment(sketch, "E197.direction1", {"start": v(0, 20.85) * mm, "end": v(20.83, 20.85) * mm, "construction": true});
            skSolve(sketch);
        }
        {
            var Q0;
            Q0 = qSketchRegion(id + "F44", true);
            extrude(context, id + "F45", {"entities" : qUnion([Q0]), "operationType" : NewBodyOperationType.REMOVE, "oppositeDirection" : true, "depth" : 25.4 * mm, "offsetDistance" : 25.4 * mm});
        }
    });
